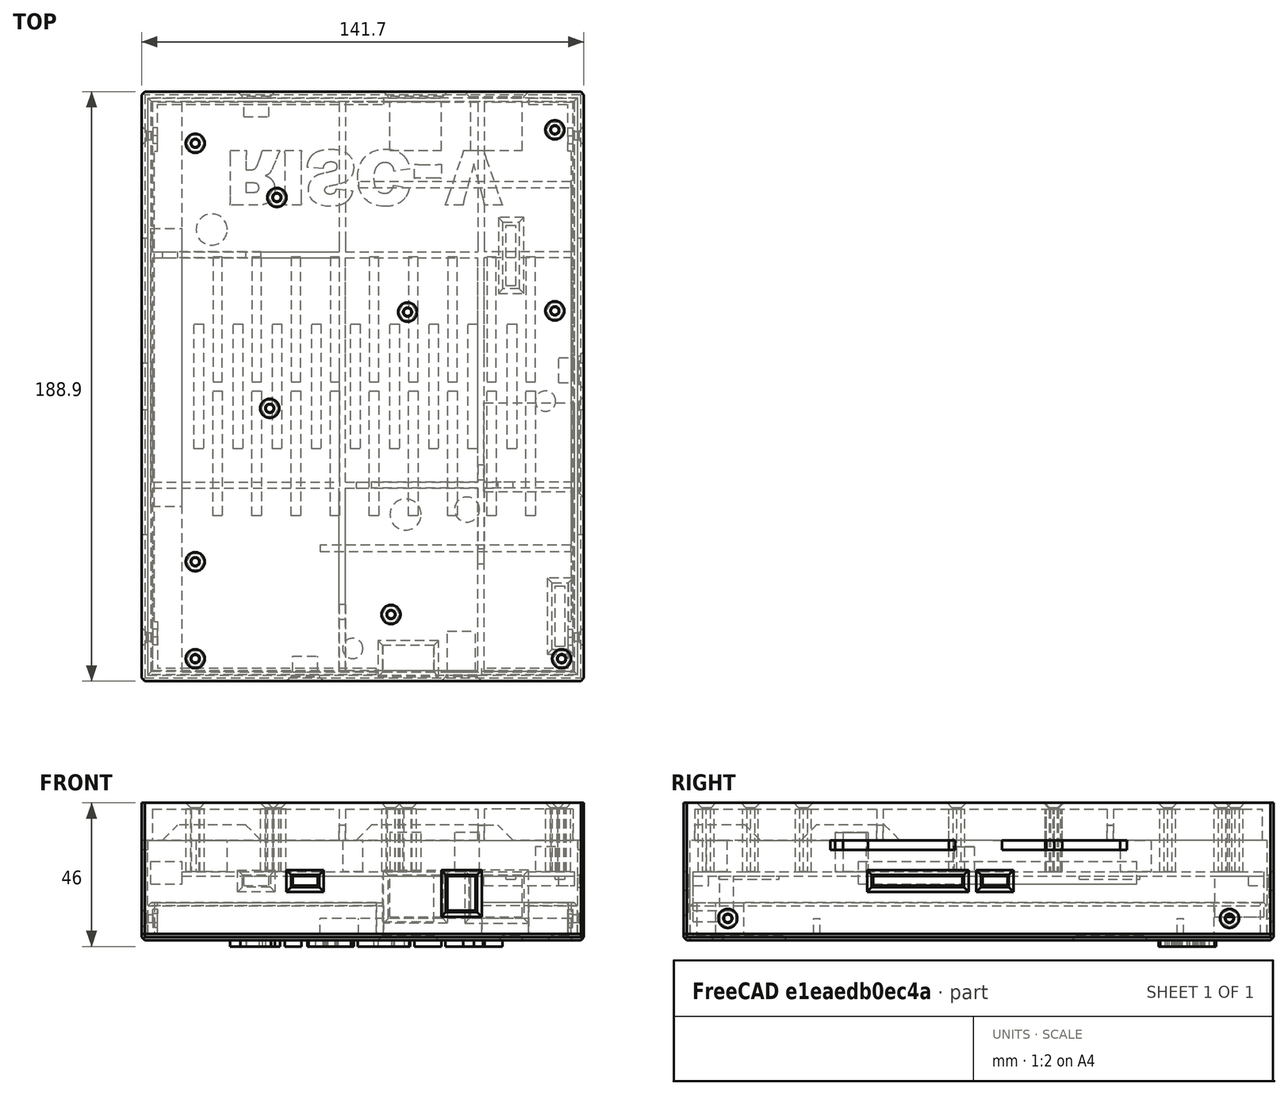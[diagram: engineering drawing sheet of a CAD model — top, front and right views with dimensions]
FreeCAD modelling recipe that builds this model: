
FCSTD DOCUMENT  (FreeCAD 0.20R29410 (Git))
Label: ICICLE_BOX
License: All rights reserved
LicenseURL: http://en.wikipedia.org/wiki/All_rights_reserved
objects: Sketcher::SketchObject×25, Part::Cylinder×15, PartDesign::Pocket×15, Part::Box×12, Part::Prism×10, Part::Cut×10, PartDesign::SubShapeBinder×10, PartDesign::Body×10, PartDesign::Pad×8, PartDesign::FeatureBase×8, PartDesign::Chamfer×7, Mesh::Feature×6, App::DocumentObjectGroup×4, PartDesign::Hole×3, PartDesign::LinearPattern×1, Part::Part2DObjectPython×1
note: 168 computed .brp shape members not serialized (recipe doc carries the construction recipe); baked Part::Feature solids carry a one-line shape summary decoded from their .brp

FEATURE [Part::Box] Box  label="MainBoard"
  AttacherType = Attacher::AttachEngine3D
  Height = 1.5
  Length = 125.7
  Placement = pos=(-4.2,-4.2,-21.5) rot=(0,0,1;0rad)
  Width = 182.9
FEATURE [Part::Box] Box001  label="PCIEX16"
  AttacherType = Attacher::AttachEngine3D
  Height = 7.3
  Length = 10
  Placement = pos=(-14.2,48.8,-24) rot=(0,0,1;0rad)
  Width = 89.1
FEATURE [Part::Box] Box002  label="J001"
  AttacherType = Attacher::AttachEngine3D
  Height = 13
  Length = 16.5
  Placement = pos=(62.3,162.9,-34.5) rot=(0,0,1;0rad)
  Width = 15.8
FEATURE [Part::Box] Box003  label="J002"
  AttacherType = Attacher::AttachEngine3D
  Height = 13
  Length = 16.5
  Placement = pos=(88.3,162.9,-34.5) rot=(0,0,1;0rad)
  Width = 15.8
FEATURE [Part::Prism] Prism  label="Spacer1"
  AttacherType = Attacher::AttachEngine3D
  Circumradius = 2.9
  FirstAngle = 0
  Height = 20
  Placement = pos=(0,0,-20) rot=(0,0,1;0rad)
  Polygon = 6
  SecondAngle = 0
FEATURE [Part::Cylinder] Cylinder  label="ScrewHole1"
  Angle = 360
  AttacherType = Attacher::AttachEngine3D
  FirstAngle = 0
  Height = 20
  Placement = pos=(0,0,-20) rot=(0,0,1;0rad)
  Radius = 1.25
  SecondAngle = 0
FEATURE [Part::Cut] Cut  label="SPC001"
  Base = -> Prism
  Tool = -> Cylinder
FEATURE [Part::Cylinder] Cylinder001  label="ScrewHole002"
  Angle = 360
  AttacherType = Attacher::AttachEngine3D
  FirstAngle = 0
  Height = 20
  Placement = pos=(0,0,-20) rot=(0,0,1;0rad)
  Radius = 1.25
  SecondAngle = 0
FEATURE [Part::Prism] Prism001  label="Spacer002"
  AttacherType = Attacher::AttachEngine3D
  Circumradius = 2.9
  FirstAngle = 0
  Height = 20
  Placement = pos=(0,0,-20) rot=(0,0,1;0rad)
  Polygon = 6
  SecondAngle = 0
FEATURE [Part::Cut] Cut001  label="SPC002"
  Base = -> Prism001
  Placement = pos=(0,31.08,0) rot=(0,0,1;0rad)
  Tool = -> Cylinder001
FEATURE [Part::Cylinder] Cylinder002  label="ScrewHole003"
  Angle = 360
  AttacherType = Attacher::AttachEngine3D
  FirstAngle = 0
  Height = 20
  Placement = pos=(0,0,-20) rot=(0,0,1;0rad)
  Radius = 1.25
  SecondAngle = 0
FEATURE [Part::Prism] Prism002  label="Spacer003"
  AttacherType = Attacher::AttachEngine3D
  Circumradius = 2.9
  FirstAngle = 0
  Height = 20
  Placement = pos=(0,0,-20) rot=(0,0,1;0rad)
  Polygon = 6
  SecondAngle = 0
FEATURE [Part::Cut] Cut002  label="SPC003"
  Base = -> Prism002
  Placement = pos=(0,165.17,0) rot=(0,0,1;0rad)
  Tool = -> Cylinder002
FEATURE [Part::Cylinder] Cylinder003  label="ScrewHole004"
  Angle = 360
  AttacherType = Attacher::AttachEngine3D
  FirstAngle = 0
  Height = 20
  Placement = pos=(0,0,-20) rot=(0,0,1;0rad)
  Radius = 1.25
  SecondAngle = 0
FEATURE [Part::Prism] Prism003  label="Spacer004"
  AttacherType = Attacher::AttachEngine3D
  Circumradius = 2.9
  FirstAngle = 0
  Height = 20
  Placement = pos=(0,0,-20) rot=(0,0,1;0rad)
  Polygon = 6
  SecondAngle = 0
FEATURE [Part::Cut] Cut003  label="SPC004"
  Base = -> Prism003
  Placement = pos=(23.86,80.23,0) rot=(0,0,1;0rad)
  Tool = -> Cylinder003
FEATURE [Part::Cylinder] Cylinder004  label="ScrewHole005"
  Angle = 360
  AttacherType = Attacher::AttachEngine3D
  FirstAngle = 0
  Height = 20
  Placement = pos=(0,0,-20) rot=(0,0,1;0rad)
  Radius = 1.25
  SecondAngle = 0
FEATURE [Part::Prism] Prism004  label="Spacer005"
  AttacherType = Attacher::AttachEngine3D
  Circumradius = 2.9
  FirstAngle = 0
  Height = 20
  Placement = pos=(0,0,-20) rot=(0,0,1;0rad)
  Polygon = 6
  SecondAngle = 0
FEATURE [Part::Cut] Cut004  label="SPC005"
  Base = -> Prism004
  Placement = pos=(26.15,147.81,0) rot=(0,0,1;0rad)
  Tool = -> Cylinder004
FEATURE [Part::Cylinder] Cylinder005  label="ScrewHole006"
  Angle = 360
  AttacherType = Attacher::AttachEngine3D
  FirstAngle = 0
  Height = 20
  Placement = pos=(0,0,-20) rot=(0,0,1;0rad)
  Radius = 1.25
  SecondAngle = 0
FEATURE [Part::Prism] Prism005  label="Spacer006"
  AttacherType = Attacher::AttachEngine3D
  Circumradius = 2.9
  FirstAngle = 0
  Height = 20
  Placement = pos=(0,0,-20) rot=(0,0,1;0rad)
  Polygon = 6
  SecondAngle = 0
FEATURE [Part::Cut] Cut005  label="SPC006"
  Base = -> Prism005
  Placement = pos=(62.71,14.17,0) rot=(0,0,1;0rad)
  Tool = -> Cylinder005
FEATURE [Part::Cylinder] Cylinder006  label="ScrewHole007"
  Angle = 360
  AttacherType = Attacher::AttachEngine3D
  FirstAngle = 0
  Height = 20
  Placement = pos=(0,0,-20) rot=(0,0,1;0rad)
  Radius = 1.25
  SecondAngle = 0
FEATURE [Part::Prism] Prism006  label="Spacer007"
  AttacherType = Attacher::AttachEngine3D
  Circumradius = 2.9
  FirstAngle = 0
  Height = 20
  Placement = pos=(0,0,-20) rot=(0,0,1;0rad)
  Polygon = 6
  SecondAngle = 0
FEATURE [Part::Cut] Cut006  label="SPC007"
  Base = -> Prism006
  Placement = pos=(68.01,111.08,0) rot=(0,0,1;0rad)
  Tool = -> Cylinder006
FEATURE [Part::Cylinder] Cylinder007  label="ScrewHole008"
  Angle = 360
  AttacherType = Attacher::AttachEngine3D
  FirstAngle = 0
  Height = 20
  Placement = pos=(0,0,-20) rot=(0,0,1;0rad)
  Radius = 1.25
  SecondAngle = 0
FEATURE [Part::Prism] Prism007  label="Spacer008"
  AttacherType = Attacher::AttachEngine3D
  Circumradius = 2.9
  FirstAngle = 0
  Height = 20
  Placement = pos=(0,0,-20) rot=(0,0,1;0rad)
  Polygon = 6
  SecondAngle = 0
FEATURE [Part::Cut] Cut007  label="SPC008"
  Base = -> Prism007
  Placement = pos=(117.35,0,0) rot=(0,0,1;0rad)
  Tool = -> Cylinder007
FEATURE [Part::Cylinder] Cylinder008  label="ScrewHole009"
  Angle = 360
  AttacherType = Attacher::AttachEngine3D
  FirstAngle = 0
  Height = 20
  Placement = pos=(0,0,-20) rot=(0,0,1;0rad)
  Radius = 1.25
  SecondAngle = 0
FEATURE [Part::Prism] Prism008  label="Spacer009"
  AttacherType = Attacher::AttachEngine3D
  Circumradius = 2.9
  FirstAngle = 0
  Height = 20
  Placement = pos=(0,0,-20) rot=(0,0,1;0rad)
  Polygon = 6
  SecondAngle = 0
FEATURE [Part::Cut] Cut008  label="SPC009"
  Base = -> Prism008
  Placement = pos=(115.19,111.46,0) rot=(0,0,1;0rad)
  Tool = -> Cylinder008
FEATURE [Part::Cylinder] Cylinder009  label="ScrewHole010"
  Angle = 360
  AttacherType = Attacher::AttachEngine3D
  FirstAngle = 0
  Height = 20
  Placement = pos=(0,0,-20) rot=(0,0,1;0rad)
  Radius = 1.25
  SecondAngle = 0
FEATURE [Part::Prism] Prism009  label="Spacer010"
  AttacherType = Attacher::AttachEngine3D
  Circumradius = 2.9
  FirstAngle = 0
  Height = 20
  Placement = pos=(0,0,-20) rot=(0,0,1;0rad)
  Polygon = 6
  SecondAngle = 0
FEATURE [Part::Cut] Cut009  label="SPC010"
  Base = -> Prism009
  Placement = pos=(115.19,169.46,0) rot=(0,0,1;0rad)
  Tool = -> Cylinder009
FEATURE [Part::Box] Box004  label="SD"
  AttacherType = Attacher::AttachEngine3D
  Height = 3
  Length = 29
  Placement = pos=(92.5,53.5,-24.5) rot=(0,0,1;0rad)
  Width = 28.5
FEATURE [Part::Box] Box005  label="DCin"
  AttacherType = Attacher::AttachEngine3D
  Height = 11
  Length = 9
  Placement = pos=(80.8,-4.2,-32.5) rot=(0,0,1;0rad)
  Width = 13
FEATURE [Part::Box] Box006  label="UART"
  AttacherType = Attacher::AttachEngine3D
  Height = 3
  Length = 8
  Placement = pos=(15.56,173.7,-24.5) rot=(0,0,1;0rad)
  Width = 5
FEATURE [Part::Box] Box007  label="OTG"
  AttacherType = Attacher::AttachEngine3D
  Height = 3
  Length = 5
  Placement = pos=(116.5,88.45,-24.5) rot=(0,0,1;0rad)
  Width = 8
FEATURE [Part::Box] Box008  label="PROG"
  AttacherType = Attacher::AttachEngine3D
  Height = 3
  Length = 8
  Placement = pos=(31.18,-4.2,-24.5) rot=(0,0,1;0rad)
  Width = 5
FEATURE [Part::Box] Box009  label="LEDArray"
  AttacherType = Attacher::AttachEngine3D
  Height = 1
  Length = 3.2
  Placement = pos=(99.59,119.55,-22.5) rot=(0,0,1;0rad)
  Width = 19.38
FEATURE [Part::Box] Box010  label="MainSW"
  AttacherType = Attacher::AttachEngine3D
  Height = 14.5
  Length = 16.5
  Placement = pos=(60,-4.2,-36) rot=(0,0,1;0rad)
  Width = 8.5
FEATURE [PartDesign::SubShapeBinder] Binder010
  BindCopyOnChange = 0
  BindMode = 0
  ClaimChildren = false
  Context = -> Body009 [Binder010.]
  Fuse = false
  MakeFace = true
  OffsetFill = false
  OffsetIntersection = false
  OffsetJoinType = 0
  OffsetOpenResult = false
  PartialLoad = false
  Relative = true
  Support = -> [Box[Face5],Box001[Face5]]
  _Version = 2
FEATURE [Sketcher::SketchObject] Sketch040
  ExternalGeometry = -> [Binder010]
  FullyConstrained = true
  MapMode = 5
  Support = -> [XY_Plane009]
  sketch-geometry (4):
    g0: LineSegment StartX=-17.2 StartY=181.7 StartZ=0 EndX=124.5 EndY=181.7 EndZ=0
    g1: LineSegment StartX=124.5 StartY=181.7 StartZ=0 EndX=124.5 EndY=-7.2 EndZ=0
    g2: LineSegment StartX=124.5 StartY=-7.2 StartZ=0 EndX=-17.2 EndY=-7.2 EndZ=0
    g3: LineSegment StartX=-17.2 StartY=-7.2 StartZ=0 EndX=-17.2 EndY=181.7 EndZ=0
  constraints (12):
    c: Coincident(g0,g1)
    c: Coincident(g1,g2)
    c: Coincident(g2,g3)
    c: Coincident(g3,g0)
    c: Horizontal(g0)
    c: Horizontal(g2)
    c: Vertical(g1)
    c: Vertical(g3)
    c: DistanceX(g0,g-3) = 3
    c: DistanceY(g-4,g0) = 3
    c: DistanceY(g1,g-4) = 3
    c: DistanceX(g-4,g0) = 3
FEATURE [PartDesign::Pad] Pad014
  Direction = (0,0,1)
  Length = 2
  Length2 = 40
  Profile = -> Sketch040
  ReferenceAxis = -> Sketch040 [N_Axis]
  Type = 4
FEATURE [Sketcher::SketchObject] Sketch041
  ExternalGeometry = -> [Pad014]
  FullyConstrained = true
  MapMode = 5
  Placement = pos=(0,0,-40) rot=(1,0,0;3.14159rad)
  Support = -> [Pad014]
  sketch-geometry (4):
    g0: LineSegment StartX=-15.2 StartY=5.2 StartZ=0 EndX=122.5 EndY=5.2 EndZ=0
    g1: LineSegment StartX=122.5 StartY=5.2 StartZ=0 EndX=122.5 EndY=-179.7 EndZ=0
    g2: LineSegment StartX=122.5 StartY=-179.7 StartZ=0 EndX=-15.2 EndY=-179.7 EndZ=0
    g3: LineSegment StartX=-15.2 StartY=-179.7 StartZ=0 EndX=-15.2 EndY=5.2 EndZ=0
  constraints (12):
    c: Coincident(g0,g1)
    c: Coincident(g1,g2)
    c: Coincident(g2,g3)
    c: Coincident(g3,g0)
    c: Horizontal(g0)
    c: Horizontal(g2)
    c: Vertical(g1)
    c: Vertical(g3)
    c: DistanceX(g-3,g0) = 2
    c: DistanceX(g0,g-3) = 2
    c: DistanceY(g0,g-3) = 2
    c: DistanceY(g-4,g1) = 2
FEATURE [PartDesign::Pocket] Pocket021
  BaseFeature = -> Pad014
  Direction = (0,0,1)
  Length = 30
  Length2 = 5
  Profile = -> Sketch041
  ReferenceAxis = -> Sketch041 [N_Axis]
  Type = 0
FEATURE [Sketcher::SketchObject] Sketch042
  ExternalGeometry = -> [Pocket021]
  FullyConstrained = true
  MapMode = 5
  Placement = pos=(0,0,-10) rot=(1,0,0;3.14159rad)
  Support = -> [Pocket021]
  sketch-geometry (4):
    g0: LineSegment StartX=-13.7 StartY=3.7 StartZ=0 EndX=121 EndY=3.7 EndZ=0
    g1: LineSegment StartX=121 StartY=3.7 StartZ=0 EndX=121 EndY=-178.2 EndZ=0
    g2: LineSegment StartX=121 StartY=-178.2 StartZ=0 EndX=-13.7 EndY=-178.2 EndZ=0
    g3: LineSegment StartX=-13.7 StartY=-178.2 StartZ=0 EndX=-13.7 EndY=3.7 EndZ=0
  constraints (12):
    c: Coincident(g0,g1)
    c: Coincident(g1,g2)
    c: Coincident(g2,g3)
    c: Coincident(g3,g0)
    c: Horizontal(g0)
    c: Horizontal(g2)
    c: Vertical(g1)
    c: Vertical(g3)
    c: DistanceX(g-3,g0) = 1.5
    c: DistanceX(g0,g-3) = 1.5
    c: DistanceY(g0,g-3) = 1.5
    c: DistanceY(g-4,g1) = 1.5
FEATURE [PartDesign::Pocket] Pocket022
  BaseFeature = -> Pocket021
  Direction = (0,0,1)
  Length = 10
  Length2 = 5
  Profile = -> Sketch042
  ReferenceAxis = -> Sketch042 [N_Axis]
  Type = 0
FEATURE [PartDesign::Body] Body009  label="BaseBox"
  Group = -> [Binder010,Sketch040,Pad014,Sketch041,Pocket021,Sketch042,Pocket022]
  Origin = -> Origin009
  Tip = -> Pocket022
FEATURE [PartDesign::SubShapeBinder] Binder011
  BindCopyOnChange = 0
  BindMode = 0
  ClaimChildren = false
  Context = -> Body010 [Binder011.]
  Fuse = false
  MakeFace = true
  OffsetFill = false
  OffsetIntersection = false
  OffsetJoinType = 0
  OffsetOpenResult = false
  PartialLoad = false
  Relative = true
  Support = -> [Body009[Pocket022.Face4]]
  _Version = 2
FEATURE [Sketcher::SketchObject] Sketch043
  ExternalGeometry = -> [Binder011]
  FullyConstrained = true
  MapMode = 5
  Placement = pos=(0,0,-40) rot=(1,0,0;3.14159rad)
  Support = -> [Binder011]
  sketch-geometry (4):
    g0: LineSegment StartX=-17.2 StartY=7.2 StartZ=0 EndX=124.5 EndY=7.2 EndZ=0
    g1: LineSegment StartX=124.5 StartY=7.2 StartZ=0 EndX=124.5 EndY=-181.7 EndZ=0
    g2: LineSegment StartX=124.5 StartY=-181.7 StartZ=0 EndX=-17.2 EndY=-181.7 EndZ=0
    g3: LineSegment StartX=-17.2 StartY=-181.7 StartZ=0 EndX=-17.2 EndY=7.2 EndZ=0
  constraints (10):
    c: Coincident(g0,g1)
    c: Coincident(g1,g2)
    c: Coincident(g2,g3)
    c: Coincident(g3,g0)
    c: Horizontal(g0)
    c: Horizontal(g2)
    c: Vertical(g1)
    c: Vertical(g3)
    c: Coincident(g0,g-3)
    c: Coincident(g1,g-4)
FEATURE [PartDesign::Pad] Pad015
  Direction = (0,0,-1)
  Length = 2
  Length2 = 10
  Profile = -> Sketch043
  ReferenceAxis = -> Sketch043 [N_Axis]
  Type = 0
FEATURE [Sketcher::SketchObject] Sketch044
  ExternalGeometry = -> [Binder011]
  FullyConstrained = true
  MapMode = 5
  Placement = pos=(0,0,-40) rot=(0,0,1;0rad)
  Support = -> [Pad015]
  sketch-geometry (4):
    g0: LineSegment StartX=-15.1 StartY=179.6 StartZ=0 EndX=122.4 EndY=179.6 EndZ=0
    g1: LineSegment StartX=122.4 StartY=179.6 StartZ=0 EndX=122.4 EndY=-5.1 EndZ=0
    g2: LineSegment StartX=122.4 StartY=-5.1 StartZ=0 EndX=-15.1 EndY=-5.1 EndZ=0
    g3: LineSegment StartX=-15.1 StartY=-5.1 StartZ=0 EndX=-15.1 EndY=179.6 EndZ=0
  constraints (12):
    c: Coincident(g0,g1)
    c: Coincident(g1,g2)
    c: Coincident(g2,g3)
    c: Coincident(g3,g0)
    c: Horizontal(g0)
    c: Horizontal(g2)
    c: Vertical(g1)
    c: Vertical(g3)
    c: DistanceY(g0,g-3) = 0.1
    c: DistanceX(g-3,g0) = 0.1
    c: DistanceX(g0,g-3) = 0.1
    c: DistanceY(g-4,g1) = 0.1
FEATURE [PartDesign::Pad] Pad016
  BaseFeature = -> Pad015
  Direction = (0,0,1)
  Length = 10
  Length2 = 10
  Profile = -> Sketch044
  ReferenceAxis = -> Sketch044 [N_Axis]
  Type = 0
FEATURE [Sketcher::SketchObject] Sketch045
  ExternalGeometry = -> [Pad016]
  FullyConstrained = true
  MapMode = 5
  Placement = pos=(0,0,-30) rot=(0,0,1;0rad)
  Support = -> [Pad016]
  sketch-geometry (4):
    g0: LineSegment StartX=-13.1 StartY=177.6 StartZ=0 EndX=120.4 EndY=177.6 EndZ=0
    g1: LineSegment StartX=120.4 StartY=177.6 StartZ=0 EndX=120.4 EndY=-3.1 EndZ=0
    g2: LineSegment StartX=120.4 StartY=-3.1 StartZ=0 EndX=-13.1 EndY=-3.1 EndZ=0
    g3: LineSegment StartX=-13.1 StartY=-3.1 StartZ=0 EndX=-13.1 EndY=177.6 EndZ=0
  constraints (12):
    c: Coincident(g0,g1)
    c: Coincident(g1,g2)
    c: Coincident(g2,g3)
    c: Coincident(g3,g0)
    c: Horizontal(g0)
    c: Horizontal(g2)
    c: Vertical(g1)
    c: Vertical(g3)
    c: DistanceX(g-3,g0) = 2
    c: DistanceX(g0,g-3) = 2
    c: DistanceY(g0,g-3) = 2
    c: DistanceY(g-4,g1) = 2
FEATURE [PartDesign::Pocket] Pocket023
  BaseFeature = -> Pad016
  Direction = (0,0,-1)
  Length = 10
  Length2 = 5
  Profile = -> Sketch045
  ReferenceAxis = -> Sketch045 [N_Axis]
  Type = 0
FEATURE [PartDesign::Body] Body010  label="LidPlate"
  Group = -> [Binder011,Sketch043,Pad015,Sketch044,Pad016,Sketch045,Pocket023]
  Origin = -> Origin010
  Tip = -> Pocket023
FEATURE [Part::Box] Box011  label="LEDArrayUser"
  AttacherType = Attacher::AttachEngine3D
  Height = 1
  Length = 3.2
  Placement = pos=(115.3,4,-22.5) rot=(0,0,1;0rad)
  Width = 19.38
FEATURE [Part::Cylinder] Cylinder010  label="C245"
  Angle = 360
  AttacherType = Attacher::AttachEngine3D
  FirstAngle = 0
  Height = 8
  Placement = pos=(112.2,82.55,-20) rot=(0,0,1;0rad)
  Radius = 3.25
  SecondAngle = 0
FEATURE [Part::Cylinder] Cylinder011  label="C482"
  Angle = 360
  AttacherType = Attacher::AttachEngine3D
  FirstAngle = 0
  Height = 12.5
  Placement = pos=(87.05,47.8,-20) rot=(0,0,1;0rad)
  Radius = 4
  SecondAngle = 0
FEATURE [Part::Cylinder] Cylinder012  label="C495"
  Angle = 360
  AttacherType = Attacher::AttachEngine3D
  FirstAngle = 0
  Height = 10
  Placement = pos=(5.29,137.53,-20) rot=(0,0,1;0rad)
  Radius = 5
  SecondAngle = 0
FEATURE [Part::Cylinder] Cylinder013  label="C527"
  Angle = 360
  AttacherType = Attacher::AttachEngine3D
  FirstAngle = 0
  Height = 12.5
  Placement = pos=(67.39,46.2,-20) rot=(0,0,1;0rad)
  Radius = 5
  SecondAngle = 0
FEATURE [Part::Cylinder] Cylinder014  label="C749"
  Angle = 360
  AttacherType = Attacher::AttachEngine3D
  FirstAngle = 0
  Height = 10
  Placement = pos=(50.45,3.29,-20) rot=(0,0,1;0rad)
  Radius = 3.25
  SecondAngle = 0
FEATURE [App::DocumentObjectGroup] Group003  label="Board"
  Group = -> [Box,Box001,Box002,Box003,Cut,Cut001,Cut002,Cut003,Cut004,Cut005,Cut006,Cut007,Cut008,Cut009,Box004,Box005,Box006,Box007,Box008,Box009,Box010,Box011,Cylinder010,Cylinder011,Cylinder012,Cylinder013,Cylinder014]
FEATURE [PartDesign::FeatureBase] Clone008
  BaseFeature = -> Body010
FEATURE [Sketcher::SketchObject] Sketch
  ExternalGeometry = -> [Clone008]
  FullyConstrained = true
  MapMode = 5
  Placement = pos=(-13.1,0,0) rot=(0.57735,0.57735,0.57735;2.0944rad)
  Support = -> [Clone008]
  sketch-geometry (8):
    g0: LineSegment StartX=-3.1 StartY=-30 StartZ=0 EndX=11.9 EndY=-30 EndZ=0
    g1: LineSegment StartX=11.9 StartY=-30 StartZ=0 EndX=11.9 EndY=-40 EndZ=0
    g2: LineSegment StartX=11.9 StartY=-40 StartZ=0 EndX=-3.1 EndY=-40 EndZ=0
    g3: LineSegment StartX=-3.1 StartY=-40 StartZ=0 EndX=-3.1 EndY=-30 EndZ=0
    g4: LineSegment StartX=177.6 StartY=-30 StartZ=0 EndX=162.6 EndY=-30 EndZ=0
    g5: LineSegment StartX=162.6 StartY=-30 StartZ=0 EndX=162.6 EndY=-40 EndZ=0
    g6: LineSegment StartX=162.6 StartY=-40 StartZ=0 EndX=177.6 EndY=-40 EndZ=0
    g7: LineSegment StartX=177.6 StartY=-40 StartZ=0 EndX=177.6 EndY=-30 EndZ=0
  constraints (22):
    c: Coincident(g0,g1)
    c: Coincident(g1,g2)
    c: Coincident(g2,g3)
    c: Coincident(g3,g0)
    c: Horizontal(g0)
    c: Horizontal(g2)
    c: Vertical(g1)
    c: Vertical(g3)
    c: Coincident(g0,g-3)
    c: PointOnObject(g1,g-4)
    c: Coincident(g4,g5)
    c: Coincident(g5,g6)
    c: Coincident(g6,g7)
    c: Coincident(g7,g4)
    c: Horizontal(g4)
    c: Horizontal(g6)
    c: Vertical(g5)
    c: Vertical(g7)
    c: Coincident(g4,g-3)
    c: PointOnObject(g5,g-4)
    c: Equal(g0,g4)
    c: Distance(g0) = 15
FEATURE [PartDesign::Pad] Pad
  BaseFeature = -> Clone008
  Direction = (1,0,0)
  Length = 1
  Length2 = 10
  Profile = -> Sketch
  ReferenceAxis = -> Sketch [N_Axis]
  Type = 0
FEATURE [Sketcher::SketchObject] Sketch067
  ExternalGeometry = -> [Pad]
  FullyConstrained = true
  MapMode = 5
  Placement = pos=(120.4,0,0) rot=(0.57735,-0.57735,-0.57735;2.0944rad)
  Support = -> [Pad]
  sketch-geometry (8):
    g0: LineSegment StartX=-177.6 StartY=-30 StartZ=0 EndX=-162.6 EndY=-30 EndZ=0
    g1: LineSegment StartX=-162.6 StartY=-30 StartZ=0 EndX=-162.6 EndY=-40 EndZ=0
    g2: LineSegment StartX=-162.6 StartY=-40 StartZ=0 EndX=-177.6 EndY=-40 EndZ=0
    g3: LineSegment StartX=-177.6 StartY=-40 StartZ=0 EndX=-177.6 EndY=-30 EndZ=0
    g4: LineSegment StartX=3.1 StartY=-30 StartZ=0 EndX=-11.9 EndY=-30 EndZ=0
    g5: LineSegment StartX=-11.9 StartY=-30 StartZ=0 EndX=-11.9 EndY=-40 EndZ=0
    g6: LineSegment StartX=-11.9 StartY=-40 StartZ=0 EndX=3.1 EndY=-40 EndZ=0
    g7: LineSegment StartX=3.1 StartY=-40 StartZ=0 EndX=3.1 EndY=-30 EndZ=0
  constraints (22):
    c: Coincident(g0,g1)
    c: Coincident(g1,g2)
    c: Coincident(g2,g3)
    c: Coincident(g3,g0)
    c: Horizontal(g0)
    c: Horizontal(g2)
    c: Vertical(g1)
    c: Vertical(g3)
    c: Coincident(g0,g-3)
    c: PointOnObject(g1,g-4)
    c: Coincident(g4,g5)
    c: Coincident(g5,g6)
    c: Coincident(g6,g7)
    c: Coincident(g7,g4)
    c: Horizontal(g4)
    c: Horizontal(g6)
    c: Vertical(g5)
    c: Vertical(g7)
    c: Coincident(g4,g-3)
    c: PointOnObject(g5,g-4)
    c: Equal(g0,g4)
    c: Distance(g0) = 15
FEATURE [PartDesign::Pad] Pad022
  BaseFeature = -> Pad
  Direction = (-1,0,0)
  Length = 1
  Length2 = 10
  Profile = -> Sketch067
  ReferenceAxis = -> Sketch067 [N_Axis]
  Type = 0
FEATURE [Sketcher::SketchObject] Sketch068
  ExternalGeometry = -> [Pad022]
  FullyConstrained = true
  MapMode = 5
  Placement = pos=(-12.1,0,0) rot=(0.57735,0.57735,0.57735;2.0944rad)
  Support = -> [Pad022]
  sketch-geometry (4):
    g0: Circle CenterX=6.9 CenterY=-35 CenterZ=0 NormalX=0 NormalY=0 NormalZ=1 AngleXU=0 Radius=5
    g1: Circle CenterX=167.6 CenterY=-35 CenterZ=0 NormalX=0 NormalY=0 NormalZ=1 AngleXU=0 Radius=5
    g2: Circle CenterX=6.9 CenterY=-35 CenterZ=0 NormalX=0 NormalY=0 NormalZ=1 AngleXU=0 Radius=1.25
    g3: Circle CenterX=167.6 CenterY=-35 CenterZ=0 NormalX=0 NormalY=0 NormalZ=1 AngleXU=0 Radius=1.25
  constraints (10):
    c: Tangent(g0,g-3)
    c: Tangent(g-4,g0)
    c: Tangent(g0,g-5)
    c: Tangent(g1,g-6)
    c: Tangent(g1,g-7)
    c: Tangent(g1,g-8)
    c: Coincident(g2,g0)
    c: Coincident(g3,g1)
    c: Equal(g2,g3)
    c: Diameter(g2) = 2.5
FEATURE [PartDesign::Pocket] Pocket
  BaseFeature = -> Pad022
  Direction = (-1,0,0)
  Length = 5
  Length2 = 5
  Midplane = true
  Profile = -> Sketch068
  ReferenceAxis = -> Sketch068 [N_Axis]
  Type = 1
FEATURE [Sketcher::SketchObject] Sketch069
  ExternalGeometry = -> [Pocket]
  FullyConstrained = true
  MapMode = 5
  Placement = pos=(-12.1,0,0) rot=(0.57735,0.57735,0.57735;2.0944rad)
  Support = -> [Pocket]
  sketch-geometry (14):
    g0: LineSegment StartX=9.45 StartY=-36.4722 StartZ=0 EndX=9.45 EndY=-33.5278 EndZ=0
    g1: LineSegment StartX=9.45 StartY=-33.5278 StartZ=0 EndX=6.9 EndY=-32.0555 EndZ=0
    g2: LineSegment StartX=6.9 StartY=-32.0555 StartZ=0 EndX=4.35 EndY=-33.5278 EndZ=0
    g3: LineSegment StartX=4.35 StartY=-33.5278 StartZ=0 EndX=4.35 EndY=-36.4722 EndZ=0
    g4: LineSegment StartX=4.35 StartY=-36.4722 StartZ=0 EndX=6.9 EndY=-37.9445 EndZ=0
    g5: LineSegment StartX=6.9 StartY=-37.9445 StartZ=0 EndX=9.45 EndY=-36.4722 EndZ=0
    g6: Circle CenterX=6.9 CenterY=-35 CenterZ=0 NormalX=0 NormalY=0 NormalZ=1 AngleXU=0 Radius=2.94449
    g7: LineSegment StartX=170.15 StartY=-36.4722 StartZ=0 EndX=170.15 EndY=-33.5278 EndZ=0
    g8: LineSegment StartX=170.15 StartY=-33.5278 StartZ=0 EndX=167.6 EndY=-32.0555 EndZ=0
    g9: LineSegment StartX=167.6 StartY=-32.0555 StartZ=0 EndX=165.05 EndY=-33.5278 EndZ=0
    g10: LineSegment StartX=165.05 StartY=-33.5278 StartZ=0 EndX=165.05 EndY=-36.4722 EndZ=0
    g11: LineSegment StartX=165.05 StartY=-36.4722 StartZ=0 EndX=167.6 EndY=-37.9445 EndZ=0
    g12: LineSegment StartX=167.6 StartY=-37.9445 StartZ=0 EndX=170.15 EndY=-36.4722 EndZ=0
    g13: Circle CenterX=167.6 CenterY=-35 CenterZ=0 NormalX=0 NormalY=0 NormalZ=1 AngleXU=0 Radius=2.94449
  constraints (32):
    c: Coincident(g0,g1)
    c: Coincident(g1,g2)
    c: Coincident(g2,g3)
    c: Coincident(g3,g4)
    c: Coincident(g4,g5)
    c: Coincident(g5,g0)
    c: Equal(g0, g1-g5) x5
    c: PointOnObject(g0,g6)
    c: PointOnObject(g1,g6)
    c: PointOnObject(g2,g6)
    c: PointOnObject(g3,g6)
    c: PointOnObject(g4,g6)
    c: PointOnObject(g5,g6)
    c: Coincident(g6,g-3)
    c: Coincident(g7,g8)
    c: Coincident(g8,g9)
    c: Coincident(g9,g10)
    c: Coincident(g10,g11)
    c: Coincident(g11,g12)
    c: Coincident(g12,g7)
    c: Equal(g7, g8-g12) x5
    c: PointOnObject(g7,g13)
    c: PointOnObject(g8,g13)
    c: PointOnObject(g9,g13)
    c: PointOnObject(g10,g13)
    c: PointOnObject(g11,g13)
    c: PointOnObject(g12,g13)
    c: Coincident(g13,g-4)
    c: Vertical(g3)
    c: Vertical(g10)
    c: Equal(g3,g10)
    c: DistanceX(g2,g0) = 5.1
FEATURE [PartDesign::Pocket] Pocket038
  BaseFeature = -> Pocket
  Direction = (-1,0,0)
  Length = 1.5
  Length2 = 5
  Profile = -> Sketch069
  ReferenceAxis = -> Sketch069 [N_Axis]
  Type = 0
FEATURE [Sketcher::SketchObject] Sketch070
  ExternalGeometry = -> [Pocket038]
  FullyConstrained = true
  MapMode = 5
  Placement = pos=(119.4,0,0) rot=(0.57735,-0.57735,-0.57735;2.0944rad)
  Support = -> [Pocket038]
  sketch-geometry (14):
    g0: LineSegment StartX=-165.05 StartY=-36.4722 StartZ=0 EndX=-165.05 EndY=-33.5278 EndZ=0
    g1: LineSegment StartX=-165.05 StartY=-33.5278 StartZ=0 EndX=-167.6 EndY=-32.0555 EndZ=0
    g2: LineSegment StartX=-167.6 StartY=-32.0555 StartZ=0 EndX=-170.15 EndY=-33.5278 EndZ=0
    g3: LineSegment StartX=-170.15 StartY=-33.5278 StartZ=0 EndX=-170.15 EndY=-36.4722 EndZ=0
    g4: LineSegment StartX=-170.15 StartY=-36.4722 StartZ=0 EndX=-167.6 EndY=-37.9445 EndZ=0
    g5: LineSegment StartX=-167.6 StartY=-37.9445 StartZ=0 EndX=-165.05 EndY=-36.4722 EndZ=0
    g6: Circle CenterX=-167.6 CenterY=-35 CenterZ=0 NormalX=0 NormalY=0 NormalZ=1 AngleXU=0 Radius=2.94449
    g7: LineSegment StartX=-4.35 StartY=-36.4722 StartZ=0 EndX=-4.35 EndY=-33.5278 EndZ=0
    g8: LineSegment StartX=-4.35 StartY=-33.5278 StartZ=0 EndX=-6.9 EndY=-32.0555 EndZ=0
    g9: LineSegment StartX=-6.9 StartY=-32.0555 StartZ=0 EndX=-9.45 EndY=-33.5278 EndZ=0
    g10: LineSegment StartX=-9.45 StartY=-33.5278 StartZ=0 EndX=-9.45 EndY=-36.4722 EndZ=0
    g11: LineSegment StartX=-9.45 StartY=-36.4722 StartZ=0 EndX=-6.9 EndY=-37.9445 EndZ=0
    g12: LineSegment StartX=-6.9 StartY=-37.9445 StartZ=0 EndX=-4.35 EndY=-36.4722 EndZ=0
    g13: Circle CenterX=-6.9 CenterY=-35 CenterZ=0 NormalX=0 NormalY=0 NormalZ=1 AngleXU=0 Radius=2.94449
  constraints (32):
    c: Coincident(g0,g1)
    c: Coincident(g1,g2)
    c: Coincident(g2,g3)
    c: Coincident(g3,g4)
    c: Coincident(g4,g5)
    c: Coincident(g5,g0)
    c: Equal(g0, g1-g5) x5
    c: PointOnObject(g0,g6)
    c: PointOnObject(g1,g6)
    c: PointOnObject(g2,g6)
    c: PointOnObject(g3,g6)
    c: PointOnObject(g4,g6)
    c: PointOnObject(g5,g6)
    c: Coincident(g6,g-4)
    c: Coincident(g7,g8)
    c: Coincident(g8,g9)
    c: Coincident(g9,g10)
    c: Coincident(g10,g11)
    c: Coincident(g11,g12)
    c: Coincident(g12,g7)
    c: Equal(g7, g8-g12) x5
    c: PointOnObject(g7,g13)
    c: PointOnObject(g8,g13)
    c: PointOnObject(g9,g13)
    c: PointOnObject(g10,g13)
    c: PointOnObject(g11,g13)
    c: PointOnObject(g12,g13)
    c: Coincident(g13,g-3)
    c: Vertical(g10)
    c: Vertical(g3)
    c: Equal(g3,g10)
    c: DistanceX(g2,g0) = 5.1
FEATURE [PartDesign::Pocket] Pocket039
  BaseFeature = -> Pocket038
  Direction = (1,0,0)
  Length = 1.5
  Length2 = 5
  Profile = -> Sketch070
  ReferenceAxis = -> Sketch070 [N_Axis]
  Type = 0
FEATURE [PartDesign::Body] Body013  label="LidPlateScrew"
  BaseFeature = -> Body010
  Group = -> [Clone008,Sketch,Pad,Sketch067,Pad022,Sketch068,Pocket,Sketch069,Pocket038,Sketch070,Pocket039]
  Origin = -> Origin013
  Tip = -> Pocket039
FEATURE [PartDesign::FeatureBase] Clone009
  BaseFeature = -> Body009
FEATURE [PartDesign::SubShapeBinder] Binder026  label="HoleOfLid"
  BindCopyOnChange = 0
  BindMode = 0
  ClaimChildren = false
  Context = -> Body014 [Binder026.]
  Fuse = false
  MakeFace = true
  OffsetFill = false
  OffsetIntersection = false
  OffsetJoinType = 0
  OffsetOpenResult = false
  PartialLoad = false
  Relative = true
  Support = -> [Body013[Pocket039.Edge26,Pocket039.Edge27,Pocket039.Edge20,Pocket039.Edge21]]
  _Version = 2
FEATURE [Sketcher::SketchObject] Sketch071
  ExternalGeometry = -> [Binder026]
  FullyConstrained = true
  MapMode = 5
  Placement = pos=(-17.2,0,0) rot=(0.57735,-0.57735,-0.57735;2.0944rad)
  Support = -> [Clone009]
  sketch-geometry (2):
    g0: Circle CenterX=-167.6 CenterY=-35 CenterZ=0 NormalX=0 NormalY=0 NormalZ=1 AngleXU=0 Radius=1.25
    g1: Circle CenterX=-6.9 CenterY=-35 CenterZ=0 NormalX=0 NormalY=0 NormalZ=1 AngleXU=0 Radius=1.25
  constraints (4):
    c: Coincident(g0,g-4)
    c: Coincident(g1,g-3)
    c: Equal(g-3,g1)
    c: Equal(g-4,g0)
FEATURE [PartDesign::Hole] Hole
  BaseFeature = -> Clone009
  CustomThreadClearance = 0
  Depth = 2
  DepthType = 0
  Diameter = 3.1
  DrillForDepth = false
  DrillPoint = 1
  DrillPointAngle = 118
  HoleCutCountersinkAngle = 90
  HoleCutCustomValues = false
  HoleCutDepth = 0
  HoleCutDiameter = 6.1
  HoleCutType = 2
  ModelThread = false
  Profile = -> Sketch071
  Tapered = false
  TaperedAngle = 90
  ThreadClass = 0
  ThreadDepth = 2
  ThreadDepthType = 0
  ThreadDirection = 0
  ThreadFit = 2
  ThreadSize = 8
  ThreadType = 1
  Threaded = false
  UseCustomThreadClearance = false
FEATURE [Sketcher::SketchObject] Sketch072
  ExternalGeometry = -> [Binder026]
  FullyConstrained = true
  MapMode = 5
  Placement = pos=(124.5,0,0) rot=(0.57735,0.57735,0.57735;2.0944rad)
  Support = -> [Hole]
  sketch-geometry (2):
    g0: Circle CenterX=6.9 CenterY=-35 CenterZ=0 NormalX=0 NormalY=0 NormalZ=1 AngleXU=0 Radius=1.25
    g1: Circle CenterX=167.6 CenterY=-35 CenterZ=0 NormalX=0 NormalY=0 NormalZ=1 AngleXU=0 Radius=1.25
  constraints (4):
    c: Coincident(g0,g-3)
    c: Equal(g-3,g0)
    c: Coincident(g1,g-4)
    c: Equal(g-4,g1)
FEATURE [PartDesign::Hole] Hole008
  BaseFeature = -> Hole
  CustomThreadClearance = 0
  Depth = 2
  DepthType = 0
  Diameter = 2.9
  DrillForDepth = false
  DrillPoint = 1
  DrillPointAngle = 118
  HoleCutCountersinkAngle = 90
  HoleCutCustomValues = false
  HoleCutDepth = 0
  HoleCutDiameter = 6.1
  HoleCutType = 2
  ModelThread = false
  Profile = -> Sketch072
  Tapered = false
  TaperedAngle = 90
  ThreadClass = 0
  ThreadDepth = 2
  ThreadDepthType = 0
  ThreadDirection = 0
  ThreadFit = 0
  ThreadSize = 8
  ThreadType = 1
  Threaded = false
  UseCustomThreadClearance = false
FEATURE [PartDesign::Body] Body014  label="BaseBoxScrew"
  BaseFeature = -> Body009
  Group = -> [Clone009,Binder026,Sketch071,Hole,Sketch072,Hole008]
  Origin = -> Origin014
  Tip = -> Hole008
FEATURE [App::DocumentObjectGroup] Group006  label="Templates"
  Group = -> [Body009,Body010,Body013,Body014]
FEATURE [PartDesign::FeatureBase] Clone010
  BaseFeature = -> Body013
FEATURE [PartDesign::SubShapeBinder] Binder  label="EthernetPorts"
  BindCopyOnChange = 0
  BindMode = 0
  ClaimChildren = false
  Context = -> Body015 [Binder.]
  Fuse = false
  MakeFace = true
  OffsetFill = false
  OffsetIntersection = false
  OffsetJoinType = 0
  OffsetOpenResult = false
  PartialLoad = false
  Relative = true
  Support = -> [Box002[Face4],Box003[Face4]]
  _Version = 2
FEATURE [PartDesign::SubShapeBinder] Binder024  label="DCandSW"
  BindCopyOnChange = 0
  BindMode = 0
  ClaimChildren = false
  Context = -> Body015 [Binder024.]
  Fuse = false
  MakeFace = true
  OffsetFill = false
  OffsetIntersection = false
  OffsetJoinType = 0
  OffsetOpenResult = false
  PartialLoad = false
  Relative = true
  Support = -> [Box010[Face3],Box005[Face3]]
  _Version = 2
FEATURE [PartDesign::SubShapeBinder] Binder025  label="LEDandSW"
  BindCopyOnChange = 0
  BindMode = 0
  ClaimChildren = false
  Context = -> Body015 [Binder025.]
  Fuse = false
  MakeFace = true
  OffsetFill = false
  OffsetIntersection = false
  OffsetJoinType = 0
  OffsetOpenResult = false
  PartialLoad = false
  Relative = true
  Support = -> [Box010[Face5],Box009[Face5],Box011[Face5]]
  _Version = 2
FEATURE [Sketcher::SketchObject] Sketch073
  ExternalGeometry = -> [Binder,Clone010]
  FullyConstrained = true
  MapMode = 5
  Placement = pos=(0,179.6,0) rot=(0,0.707107,0.707107;3.14159rad)
  Support = -> [Clone010]
  sketch-geometry (4):
    g0: LineSegment StartX=-106.8 StartY=-30 StartZ=0 EndX=-60.3 EndY=-30 EndZ=0
    g1: LineSegment StartX=-60.3 StartY=-30 StartZ=0 EndX=-60.3 EndY=-40 EndZ=0
    g2: LineSegment StartX=-60.3 StartY=-40 StartZ=0 EndX=-106.8 EndY=-40 EndZ=0
    g3: LineSegment StartX=-106.8 StartY=-40 StartZ=0 EndX=-106.8 EndY=-30 EndZ=0
  constraints (12):
    c: Coincident(g0,g1)
    c: Coincident(g1,g2)
    c: Coincident(g2,g3)
    c: Coincident(g3,g0)
    c: Horizontal(g0)
    c: Horizontal(g2)
    c: Vertical(g1)
    c: Vertical(g3)
    c: PointOnObject(g2,g-7)
    c: PointOnObject(g0,g-8)
    c: DistanceX(g0,g-3) = 2
    c: DistanceX(g-6,g0) = 2
FEATURE [PartDesign::Pocket] Pocket040
  BaseFeature = -> Clone010
  Direction = (0,-1,2e-16)
  Length = 5
  Length2 = 5
  Profile = -> Sketch073
  ReferenceAxis = -> Sketch073 [N_Axis]
  Type = 2
FEATURE [Sketcher::SketchObject] Sketch074
  ExternalGeometry = -> [Pocket040,Binder024]
  FullyConstrained = true
  MapMode = 5
  Placement = pos=(0,-5.1,0) rot=(1,0,0;1.5708rad)
  Support = -> [Pocket040]
  sketch-geometry (4):
    g0: LineSegment StartX=58 StartY=-30 StartZ=0 EndX=91.8 EndY=-30 EndZ=0
    g1: LineSegment StartX=91.8 StartY=-30 StartZ=0 EndX=91.8 EndY=-40 EndZ=0
    g2: LineSegment StartX=91.8 StartY=-40 StartZ=0 EndX=58 EndY=-40 EndZ=0
    g3: LineSegment StartX=58 StartY=-40 StartZ=0 EndX=58 EndY=-30 EndZ=0
  constraints (12):
    c: Coincident(g0,g1)
    c: Coincident(g1,g2)
    c: Coincident(g2,g3)
    c: Coincident(g3,g0)
    c: Horizontal(g0)
    c: Horizontal(g2)
    c: Vertical(g1)
    c: Vertical(g3)
    c: PointOnObject(g0,g-4)
    c: PointOnObject(g1,g-3)
    c: DistanceX(g0,g-5) = 2
    c: DistanceX(g-6,g0) = 2
FEATURE [PartDesign::Pocket] Pocket041
  BaseFeature = -> Pocket040
  Direction = (0,1,-2e-16)
  Length = 5
  Length2 = 5
  Profile = -> Sketch074
  ReferenceAxis = -> Sketch074 [N_Axis]
  Type = 2
FEATURE [Sketcher::SketchObject] Sketch075
  ExternalGeometry = -> [Binder025]
  FullyConstrained = true
  MapMode = 5
  Placement = pos=(0,0,-42) rot=(1,0,0;3.14159rad)
  Support = -> [Pocket041]
  sketch-geometry (12):
    g0: LineSegment StartX=60 StartY=4.2 StartZ=0 EndX=76.5 EndY=4.2 EndZ=0
    g1: LineSegment StartX=76.5 StartY=4.2 StartZ=0 EndX=76.5 EndY=-4.3 EndZ=0
    g2: LineSegment StartX=76.5 StartY=-4.3 StartZ=0 EndX=60 EndY=-4.3 EndZ=0
    g3: LineSegment StartX=60 StartY=-4.3 StartZ=0 EndX=60 EndY=4.2 EndZ=0
    g4: LineSegment StartX=114.3 StartY=-3 StartZ=0 EndX=119.5 EndY=-3 EndZ=0
    g5: LineSegment StartX=119.5 StartY=-3 StartZ=0 EndX=119.5 EndY=-24.38 EndZ=0
    g6: LineSegment StartX=119.5 StartY=-24.38 StartZ=0 EndX=114.3 EndY=-24.38 EndZ=0
    g7: LineSegment StartX=114.3 StartY=-24.38 StartZ=0 EndX=114.3 EndY=-3 EndZ=0
    g8: LineSegment StartX=98.59 StartY=-118.55 StartZ=0 EndX=103.79 EndY=-118.55 EndZ=0
    g9: LineSegment StartX=103.79 StartY=-118.55 StartZ=0 EndX=103.79 EndY=-139.93 EndZ=0
    g10: LineSegment StartX=103.79 StartY=-139.93 StartZ=0 EndX=98.59 EndY=-139.93 EndZ=0
    g11: LineSegment StartX=98.59 StartY=-139.93 StartZ=0 EndX=98.59 EndY=-118.55 EndZ=0
  constraints (34):
    c: Coincident(g0,g1)
    c: Coincident(g1,g2)
    c: Coincident(g2,g3)
    c: Coincident(g3,g0)
    c: Horizontal(g0)
    c: Horizontal(g2)
    c: Vertical(g1)
    c: Vertical(g3)
    c: Coincident(g0,g-3)
    c: Coincident(g1,g-4)
    c: Coincident(g4,g5)
    c: Coincident(g5,g6)
    c: Coincident(g6,g7)
    c: Coincident(g7,g4)
    c: Horizontal(g4)
    c: Horizontal(g6)
    c: Vertical(g5)
    c: Vertical(g7)
    c: Coincident(g8,g9)
    c: Coincident(g9,g10)
    c: Coincident(g10,g11)
    c: Coincident(g11,g8)
    c: Horizontal(g8)
    c: Horizontal(g10)
    c: Vertical(g9)
    c: Vertical(g11)
    c: DistanceX(g4,g-5) = 1
    c: DistanceY(g-5,g4) = 1
    c: DistanceY(g6,g-5) = 1
    c: DistanceX(g-6,g5) = 1
    c: DistanceX(g8,g-7) = 1
    c: DistanceY(g-7,g8) = 1
    c: DistanceY(g10,g-7) = 1
    c: DistanceX(g-8,g9) = 1
FEATURE [PartDesign::Pocket] Pocket042
  BaseFeature = -> Pocket041
  Direction = (0,0,1)
  Length = 5
  Length2 = 5
  Profile = -> Sketch075
  ReferenceAxis = -> Sketch075 [N_Axis]
  Type = 1
FEATURE [PartDesign::Chamfer] Chamfer
  Angle = 45
  Base = -> Pocket042 [Edge19,Edge7,Edge18,Edge3]
  BaseFeature = -> Pocket042
  ChamferType = 0
  FlipDirection = false
  Size = 1
  Size2 = 1
  SupportTransform = false
  UseAllEdges = false
FEATURE [PartDesign::Chamfer] Chamfer024
  Angle = 45
  Base = -> Chamfer [Edge5,Edge22,Edge4,Edge1]
  BaseFeature = -> Chamfer
  ChamferType = 0
  FlipDirection = false
  Size = 1
  Size2 = 1
  SupportTransform = false
  UseAllEdges = false
FEATURE [PartDesign::Chamfer] Chamfer025
  Angle = 45
  Base = -> Chamfer024 [Edge62,Edge58,Edge77,Edge82,Edge80,Edge65]
  BaseFeature = -> Chamfer024
  ChamferType = 0
  FlipDirection = false
  Size = 1
  Size2 = 1
  SupportTransform = false
  UseAllEdges = false
FEATURE [PartDesign::Chamfer] Chamfer026
  Angle = 45
  Base = -> Chamfer025 [Edge143,Edge145,Edge188,Edge140,Edge189,Edge190,Edge192,Edge191,Edge193,Edge196,Edge194,Edge195]
  BaseFeature = -> Chamfer025
  ChamferType = 0
  FlipDirection = false
  Size = 1.5
  Size2 = 1
  SupportTransform = false
  UseAllEdges = false
FEATURE [PartDesign::Body] Body015  label="ICICLE_BOX_LID_PLAIN"
  BaseFeature = -> Body013
  Group = -> [Clone010,Binder025,Binder,Binder024,Sketch073,Pocket040,Sketch074,Pocket041,Sketch075,Pocket042,Chamfer,Chamfer024,Chamfer025,Chamfer026]
  Origin = -> Origin015
  Tip = -> Chamfer026
FEATURE [PartDesign::FeatureBase] Clone
  BaseFeature = -> Body015
FEATURE [Sketcher::SketchObject] Sketch076
  ExternalGeometry = -> [Clone]
  FullyConstrained = true
  MapMode = 5
  Placement = pos=(0,0,-42) rot=(1,0,0;3.14159rad)
  Support = -> [Clone]
  sketch-geometry (22):
    g0: LineSegment StartX=-0.35 StartY=-45.75 StartZ=0 EndX=107.65 EndY=-45.75 EndZ=0
    g1: LineSegment StartX=107.65 StartY=-45.75 StartZ=0 EndX=107.65 EndY=-128.75 EndZ=0
    g2: LineSegment StartX=107.65 StartY=-128.75 StartZ=0 EndX=-0.35 EndY=-128.75 EndZ=0
    g3: LineSegment StartX=-0.35 StartY=-128.75 StartZ=0 EndX=-0.35 EndY=-45.75 EndZ=0
    g4: LineSegment StartX=-16.2 StartY=6.2 StartZ=0 EndX=-0.35 EndY=-45.75 EndZ=0
    g5: LineSegment StartX=-16.2 StartY=-180.7 StartZ=0 EndX=-0.35 EndY=-128.75 EndZ=0
    g6: LineSegment StartX=123.5 StartY=-180.7 StartZ=0 EndX=107.65 EndY=-128.75 EndZ=0
    g7: LineSegment StartX=-0.35 StartY=-67.25 StartZ=0 EndX=2.65 EndY=-67.25 EndZ=0
    g8: LineSegment StartX=2.65 StartY=-67.25 StartZ=0 EndX=2.65 EndY=-107.25 EndZ=0
    g9: LineSegment StartX=2.65 StartY=-107.25 StartZ=0 EndX=-0.35 EndY=-107.25 EndZ=0
    g10: LineSegment StartX=-0.35 StartY=-107.25 StartZ=0 EndX=-0.35 EndY=-67.25 EndZ=0
    g11: LineSegment StartX=5.65 StartY=-45.75 StartZ=0 EndX=8.65 EndY=-45.75 EndZ=0
    g12: LineSegment StartX=8.65 StartY=-45.75 StartZ=0 EndX=8.65 EndY=-85.75 EndZ=0
    g13: LineSegment StartX=8.65 StartY=-85.75 StartZ=0 EndX=5.65 EndY=-85.75 EndZ=0
    g14: LineSegment StartX=5.65 StartY=-85.75 StartZ=0 EndX=5.65 EndY=-45.75 EndZ=0
    g15: LineSegment StartX=5.65 StartY=-128.75 StartZ=0 EndX=8.65 EndY=-128.75 EndZ=0
    g16: LineSegment StartX=8.65 StartY=-128.75 StartZ=0 EndX=8.65 EndY=-88.75 EndZ=0
    g17: LineSegment StartX=8.65 StartY=-88.75 StartZ=0 EndX=5.65 EndY=-88.75 EndZ=0
    g18: LineSegment StartX=5.65 StartY=-88.75 StartZ=0 EndX=5.65 EndY=-128.75 EndZ=0
    g19: LineSegment StartX=-0.35 StartY=-45.75 StartZ=0 EndX=2.65 EndY=-67.25 EndZ=0
    g20: LineSegment StartX=-0.35 StartY=-128.75 StartZ=0 EndX=2.65 EndY=-107.25 EndZ=0
    g21: LineSegment StartX=5.65 StartY=-85.75 StartZ=0 EndX=5.65 EndY=-88.75 EndZ=0
  constraints (60):
    c: Coincident(g0,g1)
    c: Coincident(g1,g2)
    c: Coincident(g2,g3)
    c: Coincident(g3,g0)
    c: Horizontal(g0)
    c: Horizontal(g2)
    c: Vertical(g1)
    c: Vertical(g3)
    c: Distance(g0) = 108
    c: Distance(g1) = 83
    c: Coincident(g4,g-3)
    c: Coincident(g4,g0)
    c: Coincident(g5,g-4)
    c: Coincident(g5,g2)
    c: Coincident(g6,g-4)
    c: Coincident(g6,g1)
    c: Equal(g4,g5)
    c: Equal(g4,g6)
    c: Coincident(g7,g8)
    c: Coincident(g8,g9)
    c: Coincident(g9,g10)
    c: Coincident(g10,g7)
    c: Horizontal(g7)
    c: Horizontal(g9)
    c: Vertical(g8)
    c: Vertical(g10)
    c: PointOnObject(g7,g3)
    c: Coincident(g11,g12)
    c: Coincident(g12,g13)
    c: Coincident(g13,g14)
    c: Coincident(g14,g11)
    c: Horizontal(g11)
    c: Horizontal(g13)
    c: Vertical(g12)
    c: Vertical(g14)
    c: PointOnObject(g11,g0)
    c: Coincident(g15,g16)
    c: Coincident(g16,g17)
    c: Coincident(g17,g18)
    c: Coincident(g18,g15)
    c: Horizontal(g15)
    c: Horizontal(g17)
    c: Vertical(g16)
    c: Vertical(g18)
    c: PointOnObject(g15,g2)
    c: Equal(g8,g12)
    c: Equal(g8,g16)
    c: Equal(g9,g13)
    c: Equal(g9,g15)
    c: Distance(g10) = 40
    c: Distance(g7) = 3
    c: Coincident(g19,g0)
    c: Coincident(g19,g7)
    c: Coincident(g20,g2)
    c: Coincident(g20,g8)
    c: Equal(g19,g20)
    c: Coincident(g21,g13)
    c: Coincident(g21,g17)
    c: Vertical(g21)
    c: DistanceX(g7,g11) = 3
FEATURE [PartDesign::Pocket] Pocket043
  BaseFeature = -> Clone
  Direction = (0,0,1)
  Length = 5
  Length2 = 5
  Profile = -> Sketch076
  ReferenceAxis = -> Sketch076 [N_Axis]
  Type = 1
FEATURE [PartDesign::LinearPattern] LinearPattern001
  BaseFeature = -> Pocket043
  Direction = -> Sketch076 [H_Axis]
  Length = 100.3
  Occurrences = 9
  Originals = -> [Pocket043]
FEATURE [PartDesign::SubShapeBinder] Binder027  label="EthernetUpper"
  BindCopyOnChange = 0
  BindMode = 0
  ClaimChildren = false
  Context = -> Body [Binder027.]
  Fuse = false
  MakeFace = true
  OffsetFill = false
  OffsetIntersection = false
  OffsetJoinType = 0
  OffsetOpenResult = false
  PartialLoad = false
  Relative = true
  Support = -> [Box002[Face5],Box003[Face5]]
  _Version = 2
FEATURE [Sketcher::SketchObject] Sketch077
  ExternalGeometry = -> [LinearPattern001,Binder027]
  FullyConstrained = true
  MapMode = 5
  Placement = pos=(0,0,-40) rot=(0,0,1;0rad)
  Support = -> [LinearPattern001]
  sketch-geometry (8):
    g0: LineSegment StartX=120.4 StartY=152.9 StartZ=0 EndX=52.3 EndY=152.9 EndZ=0
    g1: LineSegment StartX=52.3 StartY=152.9 StartZ=0 EndX=52.3 EndY=150.9 EndZ=0
    g2: LineSegment StartX=52.3 StartY=150.9 StartZ=0 EndX=120.4 EndY=150.9 EndZ=0
    g3: LineSegment StartX=120.4 StartY=150.9 StartZ=0 EndX=120.4 EndY=152.9 EndZ=0
    g4: LineSegment StartX=120.4 StartY=36.38 StartZ=0 EndX=40 EndY=36.38 EndZ=0
    g5: LineSegment StartX=40 StartY=36.38 StartZ=0 EndX=40 EndY=34.38 EndZ=0
    g6: LineSegment StartX=40 StartY=34.38 StartZ=0 EndX=120.4 EndY=34.38 EndZ=0
    g7: LineSegment StartX=120.4 StartY=34.38 StartZ=0 EndX=120.4 EndY=36.38 EndZ=0
  constraints (24):
    c: Coincident(g0,g1)
    c: Coincident(g1,g2)
    c: Coincident(g2,g3)
    c: Coincident(g3,g0)
    c: Horizontal(g0)
    c: Horizontal(g2)
    c: Vertical(g1)
    c: Vertical(g3)
    c: PointOnObject(g0,g-3)
    c: Distance(g1) = 2
    c: DistanceX(g0,g-7) = 10
    c: DistanceY(g0,g-8) = 10
    c: Coincident(g4,g5)
    c: Coincident(g5,g6)
    c: Coincident(g6,g7)
    c: Coincident(g7,g4)
    c: Horizontal(g4)
    c: Horizontal(g6)
    c: Vertical(g5)
    c: Vertical(g7)
    c: PointOnObject(g4,g-3)
    c: Distance(g5) = 2
    c: DistanceX(g5,g-5) = 20
    c: DistanceY(g-6,g6) = 10
FEATURE [PartDesign::Pad] Pad024
  BaseFeature = -> LinearPattern001
  Direction = (0,0,1)
  Length = 5
  Length2 = 10
  Profile = -> Sketch077
  ReferenceAxis = -> Sketch077 [N_Axis]
  Type = 0
FEATURE [PartDesign::Body] Body  label="ICICLE_BOX_LID_AIRFLOW"
  BaseFeature = -> Body015
  Group = -> [Clone,Binder027,Sketch076,Pocket043,LinearPattern001,Sketch077,Pad024]
  Origin = -> Origin
  Tip = -> Pad024
FEATURE [PartDesign::FeatureBase] Clone011
  BaseFeature = -> Body
FEATURE [Part::Part2DObjectPython] ShapeString002  label="RISC-V002"  # Draft 2D object (typed FeaturePython)
  AttachmentOffset = pos=(10,-162,0) rot=(0,0,1;0rad)
  FontFile = /System/Library/Fonts/ヒラギノ角ゴシック W9.ttc
  MakeFace = true
  MapMode = 5
  Placement = pos=(10,162,-42) rot=(1,0,0;3.14159rad)
  Size = 10
  String = RISC-V
  Support = -> [Clone011]
  Tracking = 0
FEATURE [PartDesign::Pad] Pad023
  BaseFeature = -> Clone011
  Direction = (0,0,-1)
  Length = 2
  Length2 = 10
  Profile = -> ShapeString002
  ReferenceAxis = -> ShapeString002 [N_Axis]
  Type = 0
FEATURE [PartDesign::Body] Body016  label="ICICLE_BOX_LID_TEXT"
  BaseFeature = -> Body
  Group = -> [Clone011,ShapeString002,Pad023]
  Origin = -> Origin016
  Tip = -> Pad023
FEATURE [PartDesign::FeatureBase] Clone012
  BaseFeature = -> Body014
FEATURE [PartDesign::SubShapeBinder] Binder028  label="AccessPorts"
  BindCopyOnChange = 0
  BindMode = 0
  ClaimChildren = false
  Context = -> Body017 [Binder028.]
  Fuse = false
  MakeFace = true
  OffsetFill = false
  OffsetIntersection = false
  OffsetJoinType = 0
  OffsetOpenResult = false
  PartialLoad = false
  Relative = true
  Support = -> [Box002[Face4],Box003[Face4],Box004[Face2],Box005[Face3],Box006[Face4],Box007[Face2],Box008[Face3]]
  _Version = 2
FEATURE [Sketcher::SketchObject] Sketch078
  ExternalGeometry = -> [Binder028]
  FullyConstrained = true
  MapMode = 5
  Placement = pos=(0,179.7,0) rot=(1,0,0;1.5708rad)
  Support = -> [Clone012]
  sketch-geometry (12):
    g0: LineSegment StartX=15.06 StartY=-21 StartZ=0 EndX=24.06 EndY=-21 EndZ=0
    g1: LineSegment StartX=24.06 StartY=-21 StartZ=0 EndX=24.06 EndY=-25 EndZ=0
    g2: LineSegment StartX=24.06 StartY=-25 StartZ=0 EndX=15.06 EndY=-25 EndZ=0
    g3: LineSegment StartX=15.06 StartY=-25 StartZ=0 EndX=15.06 EndY=-21 EndZ=0
    g4: LineSegment StartX=61.8 StartY=-21 StartZ=0 EndX=79.3 EndY=-21 EndZ=0
    g5: LineSegment StartX=79.3 StartY=-21 StartZ=0 EndX=79.3 EndY=-35 EndZ=0
    g6: LineSegment StartX=79.3 StartY=-35 StartZ=0 EndX=61.8 EndY=-35 EndZ=0
    g7: LineSegment StartX=61.8 StartY=-35 StartZ=0 EndX=61.8 EndY=-21 EndZ=0
    g8: LineSegment StartX=87.8 StartY=-21 StartZ=0 EndX=105.3 EndY=-21 EndZ=0
    g9: LineSegment StartX=105.3 StartY=-21 StartZ=0 EndX=105.3 EndY=-35 EndZ=0
    g10: LineSegment StartX=105.3 StartY=-35 StartZ=0 EndX=87.8 EndY=-35 EndZ=0
    g11: LineSegment StartX=87.8 StartY=-35 StartZ=0 EndX=87.8 EndY=-21 EndZ=0
  constraints (36):
    c: Coincident(g0,g1)
    c: Coincident(g1,g2)
    c: Coincident(g2,g3)
    c: Coincident(g3,g0)
    c: Horizontal(g0)
    c: Horizontal(g2)
    c: Vertical(g1)
    c: Vertical(g3)
    c: Coincident(g4,g5)
    c: Coincident(g5,g6)
    c: Coincident(g6,g7)
    c: Coincident(g7,g4)
    c: Horizontal(g4)
    c: Horizontal(g6)
    c: Vertical(g5)
    c: Vertical(g7)
    c: Coincident(g8,g9)
    c: Coincident(g9,g10)
    c: Coincident(g10,g11)
    c: Coincident(g11,g8)
    c: Horizontal(g8)
    c: Horizontal(g10)
    c: Vertical(g9)
    c: Vertical(g11)
    c: DistanceX(g0,g-3) = 0.5
    c: DistanceX(g-3,g0) = 0.5
    c: DistanceY(g-3,g0) = 0.5
    c: DistanceY(g2,g-8) = 0.5
    c: DistanceX(g4,g-4) = 0.5
    c: DistanceX(g-4,g4) = 0.5
    c: DistanceX(g8,g-6) = 0.5
    c: DistanceX(g-6,g8) = 0.5
    c: DistanceY(g-4,g4) = 0.5
    c: DistanceY(g-6,g8) = 0.5
    c: DistanceY(g6,g-5) = 0.5
    c: DistanceY(g10,g-7) = 0.5
FEATURE [PartDesign::Pocket] Pocket044
  BaseFeature = -> Clone012
  Direction = (0,1,-2e-16)
  Length = 5
  Length2 = 5
  Profile = -> Sketch078
  ReferenceAxis = -> Sketch078 [N_Axis]
  Type = 2
FEATURE [Sketcher::SketchObject] Sketch079
  ExternalGeometry = -> [Binder028]
  FullyConstrained = true
  MapMode = 5
  Placement = pos=(0,-5.2,0) rot=(0,0.707107,0.707107;3.14159rad)
  Support = -> [Pocket044]
  sketch-geometry (8):
    g0: LineSegment StartX=-90.3 StartY=-21 StartZ=0 EndX=-80.3 EndY=-21 EndZ=0
    g1: LineSegment StartX=-80.3 StartY=-21 StartZ=0 EndX=-80.3 EndY=-33 EndZ=0
    g2: LineSegment StartX=-80.3 StartY=-33 StartZ=0 EndX=-90.3 EndY=-33 EndZ=0
    g3: LineSegment StartX=-90.3 StartY=-33 StartZ=0 EndX=-90.3 EndY=-21 EndZ=0
    g4: LineSegment StartX=-39.68 StartY=-21 StartZ=0 EndX=-30.68 EndY=-21 EndZ=0
    g5: LineSegment StartX=-30.68 StartY=-21 StartZ=0 EndX=-30.68 EndY=-25 EndZ=0
    g6: LineSegment StartX=-30.68 StartY=-25 StartZ=0 EndX=-39.68 EndY=-25 EndZ=0
    g7: LineSegment StartX=-39.68 StartY=-25 StartZ=0 EndX=-39.68 EndY=-21 EndZ=0
  constraints (24):
    c: Coincident(g0,g1)
    c: Coincident(g1,g2)
    c: Coincident(g2,g3)
    c: Coincident(g3,g0)
    c: Horizontal(g0)
    c: Horizontal(g2)
    c: Vertical(g1)
    c: Vertical(g3)
    c: Coincident(g4,g5)
    c: Coincident(g5,g6)
    c: Coincident(g6,g7)
    c: Coincident(g7,g4)
    c: Horizontal(g4)
    c: Horizontal(g6)
    c: Vertical(g5)
    c: Vertical(g7)
    c: DistanceX(g0,g-3) = 0.5
    c: DistanceX(g-3,g0) = 0.5
    c: DistanceX(g4,g-5) = 0.5
    c: DistanceX(g-5,g4) = 0.5
    c: DistanceY(g-3,g0) = 0.5
    c: DistanceY(g2,g-4) = 0.5
    c: DistanceY(g-5,g4) = 0.5
    c: DistanceY(g6,g-6) = 0.5
FEATURE [PartDesign::Pocket] Pocket045
  BaseFeature = -> Pocket044
  Direction = (0,-1,2e-16)
  Length = 5
  Length2 = 5
  Profile = -> Sketch079
  ReferenceAxis = -> Sketch079 [N_Axis]
  Type = 2
FEATURE [Sketcher::SketchObject] Sketch080
  ExternalGeometry = -> [Binder028]
  FullyConstrained = true
  MapMode = 5
  Placement = pos=(122.5,0,0) rot=(0.57735,-0.57735,-0.57735;2.0944rad)
  Support = -> [Pocket045]
  sketch-geometry (8):
    g0: LineSegment StartX=-96.95 StartY=-21 StartZ=0 EndX=-87.95 EndY=-21 EndZ=0
    g1: LineSegment StartX=-87.95 StartY=-21 StartZ=0 EndX=-87.95 EndY=-25 EndZ=0
    g2: LineSegment StartX=-87.95 StartY=-25 StartZ=0 EndX=-96.95 EndY=-25 EndZ=0
    g3: LineSegment StartX=-96.95 StartY=-25 StartZ=0 EndX=-96.95 EndY=-21 EndZ=0
    g4: LineSegment StartX=-82.5 StartY=-21 StartZ=0 EndX=-53 EndY=-21 EndZ=0
    g5: LineSegment StartX=-53 StartY=-21 StartZ=0 EndX=-53 EndY=-25 EndZ=0
    g6: LineSegment StartX=-53 StartY=-25 StartZ=0 EndX=-82.5 EndY=-25 EndZ=0
    g7: LineSegment StartX=-82.5 StartY=-25 StartZ=0 EndX=-82.5 EndY=-21 EndZ=0
  constraints (24):
    c: Coincident(g0,g1)
    c: Coincident(g1,g2)
    c: Coincident(g2,g3)
    c: Coincident(g3,g0)
    c: Horizontal(g0)
    c: Horizontal(g2)
    c: Vertical(g1)
    c: Vertical(g3)
    c: Coincident(g4,g5)
    c: Coincident(g5,g6)
    c: Coincident(g6,g7)
    c: Coincident(g7,g4)
    c: Horizontal(g4)
    c: Horizontal(g6)
    c: Vertical(g5)
    c: Vertical(g7)
    c: DistanceX(g0,g-4) = 0.5
    c: DistanceX(g-4,g0) = 0.5
    c: DistanceX(g4,g-5) = 0.5
    c: DistanceX(g-5,g4) = 0.5
    c: DistanceY(g-4,g0) = 0.5
    c: DistanceY(g-5,g4) = 0.5
    c: DistanceY(g2,g-3) = 0.5
    c: DistanceY(g5,g-6) = 0.5
FEATURE [PartDesign::Pocket] Pocket046
  BaseFeature = -> Pocket045
  Direction = (1,0,0)
  Length = 5
  Length2 = 5
  Profile = -> Sketch080
  ReferenceAxis = -> Sketch080 [N_Axis]
  Type = 2
FEATURE [PartDesign::SubShapeBinder] Binder029  label="FootPrint"
  BindCopyOnChange = 0
  BindMode = 0
  ClaimChildren = false
  Context = -> Body017 [Binder029.]
  Fuse = false
  MakeFace = true
  OffsetFill = false
  OffsetIntersection = false
  OffsetJoinType = 0
  OffsetOpenResult = false
  PartialLoad = false
  Relative = true
  Support = -> [Cut[Edge18],Cut001[Edge18],Cut002[Edge18],Cut003[Edge18],Cut004[Edge18],Cut005[Edge18],Cut006[Edge18],Cut007[Edge18],Cut008[Edge18],Cut009[Edge18]]
  _Version = 2
FEATURE [Sketcher::SketchObject] Sketch081
  ExternalGeometry = -> [Binder029]
  FullyConstrained = true
  MapMode = 5
  Placement = pos=(0,0,2) rot=(0,0,1;0rad)
  Support = -> [Pocket046]
  sketch-geometry (10):
    g0: Circle CenterX=0 CenterY=0 CenterZ=0 NormalX=0 NormalY=0 NormalZ=1 AngleXU=0 Radius=1.25
    g1: Circle CenterX=0 CenterY=31.08 CenterZ=0 NormalX=0 NormalY=0 NormalZ=1 AngleXU=0 Radius=1.25
    g2: Circle CenterX=62.71 CenterY=14.17 CenterZ=0 NormalX=0 NormalY=0 NormalZ=1 AngleXU=0 Radius=1.25
    g3: Circle CenterX=117.35 CenterY=0 CenterZ=0 NormalX=0 NormalY=0 NormalZ=1 AngleXU=0 Radius=1.25
    g4: Circle CenterX=23.86 CenterY=80.23 CenterZ=0 NormalX=0 NormalY=0 NormalZ=1 AngleXU=0 Radius=1.25
    g5: Circle CenterX=68.01 CenterY=111.08 CenterZ=0 NormalX=0 NormalY=0 NormalZ=1 AngleXU=0 Radius=1.25
    g6: Circle CenterX=115.19 CenterY=111.46 CenterZ=0 NormalX=0 NormalY=0 NormalZ=1 AngleXU=0 Radius=1.25
    g7: Circle CenterX=26.15 CenterY=147.81 CenterZ=0 NormalX=0 NormalY=0 NormalZ=1 AngleXU=0 Radius=1.25
    g8: Circle CenterX=115.19 CenterY=169.46 CenterZ=0 NormalX=0 NormalY=0 NormalZ=1 AngleXU=0 Radius=1.25
    g9: Circle CenterX=0 CenterY=165.17 CenterZ=0 NormalX=0 NormalY=0 NormalZ=1 AngleXU=0 Radius=1.25
  constraints (14):
    c: Coincident(g0,g-10)
    c: Coincident(g1,g-9)
    c: Coincident(g2,g-11)
    c: Coincident(g5,g-7)
    c: Coincident(g6,g-6)
    c: Coincident(g7,g-4)
    c: Coincident(g8,g-5)
    c: Coincident(g9,g-3)
    c: Equal(g0, g1-g7) x7
    c: Equal(g0,g9)
    c: Equal(g0,g8)
    c: Diameter(g0) = 2.5
    c: Coincident(g3,g-12)
    c: Coincident(g4,g-8)
FEATURE [PartDesign::Hole] Hole009
  BaseFeature = -> Pocket046
  CustomThreadClearance = 0
  Depth = 2
  DepthType = 0
  Diameter = 2.9
  DrillForDepth = false
  DrillPoint = 1
  DrillPointAngle = 118
  HoleCutCountersinkAngle = 90
  HoleCutCustomValues = false
  HoleCutDepth = 0
  HoleCutDiameter = 6.1
  HoleCutType = 2
  ModelThread = false
  Profile = -> Sketch081
  Tapered = false
  TaperedAngle = 90
  ThreadClass = 0
  ThreadDepth = 2
  ThreadDepthType = 0
  ThreadDirection = 0
  ThreadFit = 0
  ThreadSize = 8
  ThreadType = 1
  Threaded = false
  UseCustomThreadClearance = false
FEATURE [PartDesign::Chamfer] Chamfer027
  Angle = 45
  Base = -> Hole009 [Edge8,Edge7,Edge5,Edge6,Edge10,Edge12,Edge11,Edge9,Edge16,Edge14,Edge15,Edge13,Edge44,Edge41,Edge43,Edge42,Edge48,Edge47,Edge46,Edge45,Edge77,Edge78,Edge76,Edge75,Edge82,Edge79,Edge80,Edge81]
  BaseFeature = -> Hole009
  ChamferType = 0
  FlipDirection = false
  Size = 1.5
  Size2 = 1
  SupportTransform = false
  UseAllEdges = false
FEATURE [PartDesign::Chamfer] Chamfer028
  Angle = 45
  Base = -> Chamfer027 [Edge5,Edge8,Edge25,Edge52]
  BaseFeature = -> Chamfer027
  ChamferType = 0
  FlipDirection = false
  Size = 1
  Size2 = 1
  SupportTransform = false
  UseAllEdges = false
FEATURE [PartDesign::Body] Body017  label="ICICLE_BOX_BASE_PLAIN"
  BaseFeature = -> Body014
  Group = -> [Clone012,Binder028,Binder029,Sketch078,Pocket044,Sketch079,Pocket045,Sketch080,Pocket046,Sketch081,Hole009,Chamfer027,Chamfer028]
  Origin = -> Origin017
  Tip = -> Chamfer028
FEATURE [PartDesign::FeatureBase] Clone013
  BaseFeature = -> Body017
FEATURE [Sketcher::SketchObject] Sketch082
  ExternalGeometry = -> [Clone013]
  FullyConstrained = true
  MapMode = 5
  Placement = pos=(0,0,0) rot=(1,0,0;3.14159rad)
  Support = -> [Clone013]
  sketch-geometry (56):
    g0: LineSegment StartX=46.08 StartY=3.7 StartZ=0 EndX=48.08 EndY=3.7 EndZ=0
    g1: LineSegment StartX=48.08 StartY=3.7 StartZ=0 EndX=48.08 EndY=-178.2 EndZ=0
    g2: LineSegment StartX=48.08 StartY=-178.2 StartZ=0 EndX=46.08 EndY=-178.2 EndZ=0
    g3: LineSegment StartX=46.08 StartY=-178.2 StartZ=0 EndX=46.08 EndY=3.7 EndZ=0
    g4: LineSegment StartX=90.6 StartY=3.7 StartZ=0 EndX=92.6 EndY=3.7 EndZ=0
    g5: LineSegment StartX=92.6 StartY=3.7 StartZ=0 EndX=92.6 EndY=-178.2 EndZ=0
    g6: LineSegment StartX=92.6 StartY=-178.2 StartZ=0 EndX=90.6 EndY=-178.2 EndZ=0
    g7: LineSegment StartX=90.6 StartY=-178.2 StartZ=0 EndX=90.6 EndY=3.7 EndZ=0
    g8: LineSegment StartX=-13.7 StartY=-54.655 StartZ=0 EndX=121 EndY=-54.655 EndZ=0
    g9: LineSegment StartX=121 StartY=-54.655 StartZ=0 EndX=121 EndY=-56.655 EndZ=0
    g10: LineSegment StartX=121 StartY=-56.655 StartZ=0 EndX=-13.7 EndY=-56.655 EndZ=0
    g11: LineSegment StartX=-13.7 StartY=-56.655 StartZ=0 EndX=-13.7 EndY=-54.655 EndZ=0
    g12: LineSegment StartX=-13.7 StartY=-128.445 StartZ=0 EndX=121 EndY=-128.445 EndZ=0
    g13: LineSegment StartX=121 StartY=-128.445 StartZ=0 EndX=121 EndY=-130.445 EndZ=0
    g14: LineSegment StartX=121 StartY=-130.445 StartZ=0 EndX=-13.7 EndY=-130.445 EndZ=0
    g15: LineSegment StartX=-13.7 StartY=-130.445 StartZ=0 EndX=-13.7 EndY=-128.445 EndZ=0
    g16: LineSegment StartX=0 StartY=-31.08 StartZ=0 EndX=0 EndY=-54.655 EndZ=0
    g17: LineSegment StartX=23.86 StartY=-80.23 StartZ=0 EndX=23.86 EndY=-56.655 EndZ=0
    g18: LineSegment StartX=26.15 StartY=-147.81 StartZ=0 EndX=26.15 EndY=-130.445 EndZ=0
    g19: LineSegment StartX=68.01 StartY=-111.08 StartZ=0 EndX=68.01 EndY=-128.445 EndZ=0
    g20: LineSegment StartX=26.15 StartY=-147.81 StartZ=0 EndX=46.08 EndY=-147.81 EndZ=0
    g21: LineSegment StartX=68.01 StartY=-111.08 StartZ=0 EndX=48.08 EndY=-111.08 EndZ=0
    g22: LineSegment StartX=68.01 StartY=-111.08 StartZ=0 EndX=90.6 EndY=-111.08 EndZ=0
    g23: LineSegment StartX=115.19 StartY=-111.46 StartZ=0 EndX=92.6 EndY=-111.46 EndZ=0
    g24: LineSegment StartX=-13.7 StartY=-54.655 StartZ=0 EndX=-13.7 EndY=-56.655 EndZ=0
    g25: LineSegment StartX=-13.7 StartY=-54.655 StartZ=0 EndX=46.08 EndY=-54.655 EndZ=0
    g26: LineSegment StartX=-13.7 StartY=-56.655 StartZ=0 EndX=46.08 EndY=-56.655 EndZ=0
    g27: LineSegment StartX=46.08 StartY=3.7 StartZ=0 EndX=48.08 EndY=3.7 EndZ=0
    g28: LineSegment StartX=46.08 StartY=3.7 StartZ=0 EndX=46.08 EndY=-54.655 EndZ=0
    g29: LineSegment StartX=48.08 StartY=3.7 StartZ=0 EndX=48.08 EndY=-54.655 EndZ=0
    g30: LineSegment StartX=90.6 StartY=3.7 StartZ=0 EndX=92.6 EndY=3.7 EndZ=0
    g31: LineSegment StartX=90.6 StartY=3.7 StartZ=0 EndX=90.6 EndY=-54.655 EndZ=0
    g32: LineSegment StartX=92.6 StartY=3.7 StartZ=0 EndX=92.6 EndY=-54.655 EndZ=0
    g33: LineSegment StartX=121 StartY=-54.655 StartZ=0 EndX=121 EndY=-56.655 EndZ=0
    g34: LineSegment StartX=121 StartY=-54.655 StartZ=0 EndX=92.6 EndY=-54.655 EndZ=0
    g35: LineSegment StartX=121 StartY=-56.655 StartZ=0 EndX=92.6 EndY=-56.655 EndZ=0
    g36: LineSegment StartX=121 StartY=-128.445 StartZ=0 EndX=121 EndY=-130.445 EndZ=0
    g37: LineSegment StartX=121 StartY=-128.445 StartZ=0 EndX=92.6 EndY=-128.445 EndZ=0
    g38: LineSegment StartX=121 StartY=-130.445 StartZ=0 EndX=92.6 EndY=-130.445 EndZ=0
    g39: LineSegment StartX=92.6 StartY=-178.2 StartZ=0 EndX=90.6 EndY=-178.2 EndZ=0
    g40: LineSegment StartX=92.6 StartY=-178.2 StartZ=0 EndX=92.6 EndY=-130.445 EndZ=0
    g41: LineSegment StartX=90.6 StartY=-178.2 StartZ=0 EndX=90.6 EndY=-130.445 EndZ=0
    g42: LineSegment StartX=48.08 StartY=-178.2 StartZ=0 EndX=46.08 EndY=-178.2 EndZ=0
    g43: LineSegment StartX=48.08 StartY=-178.2 StartZ=0 EndX=48.08 EndY=-130.445 EndZ=0
    g44: LineSegment StartX=46.08 StartY=-178.2 StartZ=0 EndX=46.08 EndY=-130.445 EndZ=0
    g45: LineSegment StartX=-13.7 StartY=-128.445 StartZ=0 EndX=-13.7 EndY=-130.445 EndZ=0
    g46: LineSegment StartX=-13.7 StartY=-128.445 StartZ=0 EndX=46.08 EndY=-128.445 EndZ=0
    g47: LineSegment StartX=-13.7 StartY=-130.445 StartZ=0 EndX=46.08 EndY=-130.445 EndZ=0
    g48: LineSegment StartX=48.08 StartY=-54.655 StartZ=0 EndX=90.6 EndY=-54.655 EndZ=0
    g49: LineSegment StartX=46.08 StartY=-128.445 StartZ=0 EndX=46.08 EndY=-56.655 EndZ=0
    g50: LineSegment StartX=48.08 StartY=-130.445 StartZ=0 EndX=90.6 EndY=-130.445 EndZ=0
    g51: LineSegment StartX=92.6 StartY=-56.655 StartZ=0 EndX=92.6 EndY=-128.445 EndZ=0
    g52: LineSegment StartX=48.08 StartY=-56.655 StartZ=0 EndX=90.6 EndY=-56.655 EndZ=0
    g53: LineSegment StartX=48.08 StartY=-128.445 StartZ=0 EndX=90.6 EndY=-128.445 EndZ=0
    g54: LineSegment StartX=48.08 StartY=-56.655 StartZ=0 EndX=48.08 EndY=-128.445 EndZ=0
    g55: LineSegment StartX=90.6 StartY=-56.655 StartZ=0 EndX=90.6 EndY=-128.445 EndZ=0
  constraints (153):
    c: Coincident(g0,g1)
    c: Coincident(g1,g2)
    c: Coincident(g2,g3)
    c: Coincident(g3,g0)
    c: Horizontal(g0)
    c: Horizontal(g2)
    c: Vertical(g1)
    c: Vertical(g3)
    c: PointOnObject(g0,g-8)
    c: PointOnObject(g1,g-9)
    c: Coincident(g4,g5)
    c: Coincident(g5,g6)
    c: Coincident(g6,g7)
    c: Coincident(g7,g4)
    c: Horizontal(g4)
    c: Horizontal(g6)
    c: Vertical(g5)
    c: Vertical(g7)
    c: PointOnObject(g4,g-8)
    c: PointOnObject(g5,g-9)
    c: Coincident(g8,g9)
    c: Coincident(g9,g10)
    c: Coincident(g10,g11)
    c: Coincident(g11,g8)
    c: Horizontal(g8)
    c: Horizontal(g10)
    c: Vertical(g9)
    c: Vertical(g11)
    c: PointOnObject(g8,g-10)
    c: PointOnObject(g9,g-11)
    c: Coincident(g12,g13)
    c: Coincident(g13,g14)
    c: Coincident(g14,g15)
    c: Coincident(g15,g12)
    c: Horizontal(g12)
    c: Horizontal(g14)
    c: Vertical(g13)
    c: Vertical(g15)
    c: PointOnObject(g12,g-10)
    c: PointOnObject(g13,g-11)
    c: Equal(g11,g0)
    c: Equal(g11,g4)
    c: Equal(g11,g15)
    c: Distance(g11) = 2
    c: Coincident(g16,g-3)
    c: PointOnObject(g16,g8)
    c: Vertical(g16)
    c: Coincident(g17,g-4)
    c: PointOnObject(g17,g10)
    c: Vertical(g17)
    c: Equal(g16,g17)
    c: Coincident(g18,g-5)
    c: PointOnObject(g18,g14)
    c: Vertical(g18)
    c: Coincident(g19,g-6)
    c: PointOnObject(g19,g12)
    c: Vertical(g19)
    c: Equal(g18,g19)
    c: Coincident(g20,g18)
    c: PointOnObject(g20,g3)
    c: Horizontal(g20)
    c: Coincident(g21,g19)
    c: PointOnObject(g21,g1)
    c: Horizontal(g21)
    c: Equal(g20,g21)
    c: Coincident(g22,g19)
    c: PointOnObject(g22,g7)
    c: Horizontal(g22)
    c: Coincident(g23,g-7)
    c: PointOnObject(g23,g5)
    c: Horizontal(g23)
    c: Equal(g22,g23)
    c: Coincident(g24,g8)
    c: Coincident(g24,g10)
    c: Coincident(g25,g24)
    c: PointOnObject(g25,g8)
    c: PointOnObject(g26,g-10)
    c: PointOnObject(g26,g10)
    c: Horizontal(g26)
    c: Coincident(g27,g0)
    c: Coincident(g27,g0)
    c: Coincident(g28,g27)
    c: PointOnObject(g28,g3)
    c: Coincident(g29,g27)
    c: PointOnObject(g29,g1)
    c: Coincident(g30,g4)
    c: Coincident(g30,g4)
    c: Coincident(g31,g30)
    c: PointOnObject(g31,g7)
    c: Coincident(g32,g30)
    c: PointOnObject(g32,g5)
    c: Coincident(g33,g8)
    c: Coincident(g33,g9)
    c: Coincident(g34,g33)
    c: PointOnObject(g34,g8)
    c: Coincident(g35,g33)
    c: PointOnObject(g35,g10)
    c: Coincident(g36,g12)
    c: Coincident(g36,g13)
    c: Coincident(g37,g36)
    c: PointOnObject(g37,g12)
    c: Coincident(g38,g36)
    c: PointOnObject(g38,g14)
    c: Coincident(g39,g5)
    c: Coincident(g39,g6)
    c: Coincident(g40,g39)
    c: PointOnObject(g40,g5)
    c: Coincident(g41,g39)
    c: PointOnObject(g41,g7)
    c: Coincident(g42,g1)
    c: Coincident(g42,g2)
    c: Coincident(g43,g42)
    c: PointOnObject(g43,g1)
    c: Coincident(g44,g42)
    c: PointOnObject(g44,g3)
    c: Coincident(g45,g12)
    c: Coincident(g45,g14)
    c: Coincident(g46,g45)
    c: PointOnObject(g46,g12)
    c: Coincident(g47,g45)
    c: PointOnObject(g47,g14)
    c: Coincident(g25,g28)
    c: Coincident(g32,g34)
    c: Coincident(g47,g44)
    c: Coincident(g40,g38)
    c: Coincident(g48,g29)
    c: Coincident(g48,g31)
    c: Horizontal(g48)
    c: Coincident(g49,g46)
    c: Coincident(g49,g26)
    c: Vertical(g49)
    c: Coincident(g50,g43)
    c: Coincident(g50,g41)
    c: Horizontal(g50)
    c: PointOnObject(g26,g3)
    c: PointOnObject(g29,g8)
    c: PointOnObject(g43,g14)
    c: Coincident(g51,g35)
    c: Coincident(g51,g37)
    c: Vertical(g51)
    c: PointOnObject(g37,g5)
    c: PointOnObject(g52,g1)
    c: PointOnObject(g52,g7)
    c: PointOnObject(g53,g1)
    c: PointOnObject(g53,g7)
    c: PointOnObject(g52,g10)
    c: PointOnObject(g53,g12)
    c: PointOnObject(g52,g10)
    c: PointOnObject(g53,g12)
    c: Coincident(g54,g52)
    c: Coincident(g54,g53)
    c: Coincident(g55,g52)
    c: Coincident(g55,g53)
FEATURE [PartDesign::Pad] Pad025
  BaseFeature = -> Clone013
  Direction = (0,0,-1)
  Length = 10
  Length2 = 10
  Profile = -> Sketch082
  ReferenceAxis = -> Sketch082 [N_Axis]
  Type = 0
FEATURE [PartDesign::SubShapeBinder] Binder030  label="CapasitorBackside"
  BindCopyOnChange = 0
  BindMode = 0
  ClaimChildren = false
  Context = -> Body018 [Binder030.]
  Fuse = false
  MakeFace = true
  OffsetFill = false
  OffsetIntersection = false
  OffsetJoinType = 0
  OffsetOpenResult = false
  PartialLoad = false
  Relative = true
  Support = -> [Cylinder010[Face3],Cylinder011[Face3],Cylinder012[Face3],Cylinder013[Face3],Cylinder014[Face3]]
  _Version = 2
FEATURE [Sketcher::SketchObject] Sketch083
  ExternalGeometry = -> [Pad025,Binder030]
  FullyConstrained = true
  MapMode = 5
  Placement = pos=(0,0,-10) rot=(1,0,0;3.14159rad)
  Support = -> [Pad025]
  sketch-geometry (36):
    g0: LineSegment StartX=47.2 StartY=-0.04 StartZ=0 EndX=53.7 EndY=-0.04 EndZ=0
    g1: LineSegment StartX=53.7 StartY=-0.04 StartZ=0 EndX=53.7 EndY=-6.54 EndZ=0
    g2: LineSegment StartX=53.7 StartY=-6.54 StartZ=0 EndX=47.2 EndY=-6.54 EndZ=0
    g3: LineSegment StartX=47.2 StartY=-6.54 StartZ=0 EndX=47.2 EndY=-0.04 EndZ=0
    g4: LineSegment StartX=62.39 StartY=-41.2 StartZ=0 EndX=72.39 EndY=-41.2 EndZ=0
    g5: LineSegment StartX=72.39 StartY=-41.2 StartZ=0 EndX=72.39 EndY=-51.2 EndZ=0
    g6: LineSegment StartX=72.39 StartY=-51.2 StartZ=0 EndX=62.39 EndY=-51.2 EndZ=0
    g7: LineSegment StartX=62.39 StartY=-51.2 StartZ=0 EndX=62.39 EndY=-41.2 EndZ=0
    g8: LineSegment StartX=83.05 StartY=-43.8 StartZ=0 EndX=91.05 EndY=-43.8 EndZ=0
    g9: LineSegment StartX=91.05 StartY=-43.8 StartZ=0 EndX=91.05 EndY=-51.8 EndZ=0
    g10: LineSegment StartX=91.05 StartY=-51.8 StartZ=0 EndX=83.05 EndY=-51.8 EndZ=0
    g11: LineSegment StartX=83.05 StartY=-51.8 StartZ=0 EndX=83.05 EndY=-43.8 EndZ=0
    g12: LineSegment StartX=108.95 StartY=-79.3 StartZ=0 EndX=115.45 EndY=-79.3 EndZ=0
    g13: LineSegment StartX=115.45 StartY=-79.3 StartZ=0 EndX=115.45 EndY=-85.8 EndZ=0
    g14: LineSegment StartX=115.45 StartY=-85.8 StartZ=0 EndX=108.95 EndY=-85.8 EndZ=0
    g15: LineSegment StartX=108.95 StartY=-85.8 StartZ=0 EndX=108.95 EndY=-79.3 EndZ=0
    g16: LineSegment StartX=0.29 StartY=-132.53 StartZ=0 EndX=10.29 EndY=-132.53 EndZ=0
    g17: LineSegment StartX=10.29 StartY=-132.53 StartZ=0 EndX=10.29 EndY=-142.53 EndZ=0
    g18: LineSegment StartX=10.29 StartY=-142.53 StartZ=0 EndX=0.29 EndY=-142.53 EndZ=0
    g19: LineSegment StartX=0.29 StartY=-142.53 StartZ=0 EndX=0.29 EndY=-132.53 EndZ=0
    g20: LineSegment StartX=41.2 StartY=3.7 StartZ=0 EndX=59.7 EndY=3.7 EndZ=0
    g21: LineSegment StartX=59.7 StartY=3.7 StartZ=0 EndX=59.7 EndY=-12.54 EndZ=0
    g22: LineSegment StartX=59.7 StartY=-12.54 StartZ=0 EndX=41.2 EndY=-12.54 EndZ=0
    g23: LineSegment StartX=41.2 StartY=-12.54 StartZ=0 EndX=41.2 EndY=3.7 EndZ=0
    g24: LineSegment StartX=56.39 StartY=-35.2 StartZ=0 EndX=97.05 EndY=-35.2 EndZ=0
    g25: LineSegment StartX=97.05 StartY=-35.2 StartZ=0 EndX=97.05 EndY=-57.2 EndZ=0
    g26: LineSegment StartX=97.05 StartY=-57.2 StartZ=0 EndX=56.39 EndY=-57.2 EndZ=0
    g27: LineSegment StartX=56.39 StartY=-57.2 StartZ=0 EndX=56.39 EndY=-35.2 EndZ=0
    g28: LineSegment StartX=121 StartY=-73.3 StartZ=0 EndX=102.95 EndY=-73.3 EndZ=0
    g29: LineSegment StartX=102.95 StartY=-73.3 StartZ=0 EndX=102.95 EndY=-91.8 EndZ=0
    g30: LineSegment StartX=102.95 StartY=-91.8 StartZ=0 EndX=121 EndY=-91.8 EndZ=0
    g31: LineSegment StartX=121 StartY=-91.8 StartZ=0 EndX=121 EndY=-73.3 EndZ=0
    g32: LineSegment StartX=-5.71 StartY=-126.53 StartZ=0 EndX=16.29 EndY=-126.53 EndZ=0
    g33: LineSegment StartX=16.29 StartY=-126.53 StartZ=0 EndX=16.29 EndY=-148.53 EndZ=0
    g34: LineSegment StartX=16.29 StartY=-148.53 StartZ=0 EndX=-5.71 EndY=-148.53 EndZ=0
    g35: LineSegment StartX=-5.71 StartY=-148.53 StartZ=0 EndX=-5.71 EndY=-126.53 EndZ=0
  constraints (109):
    c: Coincident(g0,g1)
    c: Coincident(g1,g2)
    c: Coincident(g2,g3)
    c: Coincident(g3,g0)
    c: Horizontal(g0)
    c: Horizontal(g2)
    c: Vertical(g1)
    c: Vertical(g3)
    c: Coincident(g4,g5)
    c: Coincident(g5,g6)
    c: Coincident(g6,g7)
    c: Coincident(g7,g4)
    c: Horizontal(g4)
    c: Horizontal(g6)
    c: Vertical(g5)
    c: Vertical(g7)
    c: Coincident(g8,g9)
    c: Coincident(g9,g10)
    c: Coincident(g10,g11)
    c: Coincident(g11,g8)
    c: Horizontal(g8)
    c: Horizontal(g10)
    c: Vertical(g9)
    c: Vertical(g11)
    c: Coincident(g12,g13)
    c: Coincident(g13,g14)
    c: Coincident(g14,g15)
    c: Coincident(g15,g12)
    c: Horizontal(g12)
    c: Horizontal(g14)
    c: Vertical(g13)
    c: Vertical(g15)
    c: Coincident(g16,g17)
    c: Coincident(g17,g18)
    c: Coincident(g18,g19)
    c: Coincident(g19,g16)
    c: Horizontal(g16)
    c: Horizontal(g18)
    c: Vertical(g17)
    c: Vertical(g19)
    c: Tangent(g-8,g0)
    c: Tangent(g-8,g3)
    c: Tangent(g-8,g1)
    c: Tangent(g-8,g2)
    c: Tangent(g-9,g4)
    c: Tangent(g-9,g7)
    c: Tangent(g-9,g6)
    c: Tangent(g-9,g5)
    c: Tangent(g-10,g8)
    c: Tangent(g-10,g11)
    c: Tangent(g-10,g10)
    c: Tangent(g-10,g9)
    c: Tangent(g-11,g15)
    c: Tangent(g-11,g12)
    c: Tangent(g-11,g13)
    c: Tangent(g-11,g14)
    c: Tangent(g-12,g16)
    c: Tangent(g-12,g19)
    c: Tangent(g-12,g18)
    c: Tangent(g-12,g17)
    c: Coincident(g20,g21)
    c: Coincident(g21,g22)
    c: Coincident(g22,g23)
    c: Coincident(g23,g20)
    c: Horizontal(g20)
    c: Horizontal(g22)
    c: Vertical(g21)
    c: Vertical(g23)
    c: PointOnObject(g20,g-3)
    c: Coincident(g24,g25)
    c: Coincident(g25,g26)
    c: Coincident(g26,g27)
    c: Coincident(g27,g24)
    c: Horizontal(g24)
    c: Horizontal(g26)
    c: Vertical(g25)
    c: Vertical(g27)
    c: Coincident(g28,g29)
    c: Coincident(g29,g30)
    c: Coincident(g30,g31)
    c: Coincident(g31,g28)
    c: Horizontal(g28)
    c: Horizontal(g30)
    c: Vertical(g29)
    c: Vertical(g31)
    c: PointOnObject(g28,g-5)
    c: Coincident(g32,g33)
    c: Coincident(g33,g34)
    c: Coincident(g34,g35)
    c: Coincident(g35,g32)
    c: Horizontal(g32)
    c: Horizontal(g34)
    c: Vertical(g33)
    c: Vertical(g35)
    c: DistanceY(g22,g2) = 6
    c: DistanceX(g20,g0) = 6
    c: DistanceX(g0,g20) = 6
    c: DistanceX(g24,g4) = 6
    c: DistanceX(g8,g24) = 6
    c: DistanceY(g4,g24) = 6
    c: DistanceY(g26,g6) = 6
    c: DistanceX(g28,g12) = 6
    c: DistanceY(g12,g28) = 6
    c: DistanceY(g29,g14) = 6
    c: DistanceX(g13,g30) = 5.55
    c: DistanceX(g32,g16) = 6
    c: DistanceX(g16,g32) = 6
    c: DistanceY(g16,g32) = 6
    c: DistanceY(g33,g17) = 6
FEATURE [PartDesign::Pocket] Pocket047
  BaseFeature = -> Pad025
  Direction = (0,0,1)
  Length = 5
  Length2 = 5
  Profile = -> Sketch083
  ReferenceAxis = -> Sketch083 [N_Axis]
  Type = 0
FEATURE [PartDesign::Chamfer] Chamfer029
  Angle = 45
  Base = -> Pocket047 [Edge316,Edge292,Edge284,Edge321,Edge324,Edge306,Edge340]
  BaseFeature = -> Pocket047
  ChamferType = 0
  FlipDirection = false
  Size = 4.8
  Size2 = 1
  SupportTransform = false
  UseAllEdges = false
FEATURE [PartDesign::Body] Body018  label="ICICLE_BOX_BASE_RIBS"
  Group = -> [Clone013,Binder030,Sketch082,Pad025,Sketch083,Pocket047,Chamfer029]
  Origin = -> Origin018
  Tip = -> Chamfer029
FEATURE [PartDesign::FeatureBase] Clone014
  BaseFeature = -> Body018
FEATURE [Sketcher::SketchObject] Sketch084
  ExternalGeometry = -> [Clone014]
  FullyConstrained = true
  MapMode = 5
  Placement = pos=(-15.2,0,0) rot=(0.57735,0.57735,0.57735;2.0944rad)
  Support = -> [Clone014]
  sketch-geometry (10):
    g0: LineSegment StartX=39.75 StartY=-10 StartZ=0 EndX=79.75 EndY=-10 EndZ=0
    g1: LineSegment StartX=79.75 StartY=-10 StartZ=0 EndX=79.75 EndY=-13 EndZ=0
    g2: LineSegment StartX=79.75 StartY=-13 StartZ=0 EndX=39.75 EndY=-13 EndZ=0
    g3: LineSegment StartX=39.75 StartY=-13 StartZ=0 EndX=39.75 EndY=-10 EndZ=0
    g4: LineSegment StartX=94.75 StartY=-10 StartZ=0 EndX=134.75 EndY=-10 EndZ=0
    g5: LineSegment StartX=134.75 StartY=-10 StartZ=0 EndX=134.75 EndY=-13 EndZ=0
    g6: LineSegment StartX=134.75 StartY=-13 StartZ=0 EndX=94.75 EndY=-13 EndZ=0
    g7: LineSegment StartX=94.75 StartY=-13 StartZ=0 EndX=94.75 EndY=-10 EndZ=0
    g8: LineSegment StartX=-5.2 StartY=-10 StartZ=0 EndX=39.75 EndY=-13 EndZ=0
    g9: LineSegment StartX=179.7 StartY=-10 StartZ=0 EndX=134.75 EndY=-13 EndZ=0
  constraints (28):
    c: Coincident(g0,g1)
    c: Coincident(g1,g2)
    c: Coincident(g2,g3)
    c: Coincident(g3,g0)
    c: Horizontal(g0)
    c: Horizontal(g2)
    c: Vertical(g1)
    c: Vertical(g3)
    c: PointOnObject(g0,g-3)
    c: Coincident(g4,g5)
    c: Coincident(g5,g6)
    c: Coincident(g6,g7)
    c: Coincident(g7,g4)
    c: Horizontal(g4)
    c: Horizontal(g6)
    c: Vertical(g5)
    c: Vertical(g7)
    c: PointOnObject(g4,g-3)
    c: Equal(g1,g5)
    c: Distance(g3) = 3
    c: Equal(g2,g6)
    c: Distance(g0) = 40
    c: DistanceX(g0,g4) = 15
    c: Coincident(g8,g-3)
    c: Coincident(g8,g2)
    c: Coincident(g9,g-3)
    c: Coincident(g9,g5)
    c: Equal(g8,g9)
FEATURE [PartDesign::Pocket] Pocket048
  BaseFeature = -> Clone014
  Direction = (-1,0,0)
  Length = 5
  Length2 = 5
  Midplane = true
  Profile = -> Sketch084
  ReferenceAxis = -> Sketch084 [N_Axis]
  Type = 1
FEATURE [PartDesign::Body] Body019  label="ICICLE_BOX_BASE_AIRFLOW"
  Group = -> [Clone014,Sketch084,Pocket048]
  Origin = -> Origin019
  Tip = -> Pocket048
FEATURE [App::DocumentObjectGroup] Group007  label="Products"
  Group = -> [Body015,Body,Body016,Body017,Body018,Body019]
FEATURE [Mesh::Feature] Mesh015  label="ICICLE_BOX_LID_PLAIN_MESH"
FEATURE [Mesh::Feature] Mesh016  label="ICICLE_BOX_LID_AIRFLOW_MESH"
FEATURE [Mesh::Feature] Mesh017  label="ICICLE_BOX_LID_TEXT_MESH"
FEATURE [Mesh::Feature] Mesh018  label="ICICLE_BOX_BASE_PLAIN_MESH"
FEATURE [Mesh::Feature] Mesh019  label="ICICLE_BOX_BASE_RIBS_MESH"
FEATURE [Mesh::Feature] Mesh020  label="ICICLE_BOX_BASE_AIRFLOW_MESH"
FEATURE [App::DocumentObjectGroup] Group  label="Meshes"
  Group = -> [Mesh015,Mesh016,Mesh017,Mesh018,Mesh019,Mesh020]
